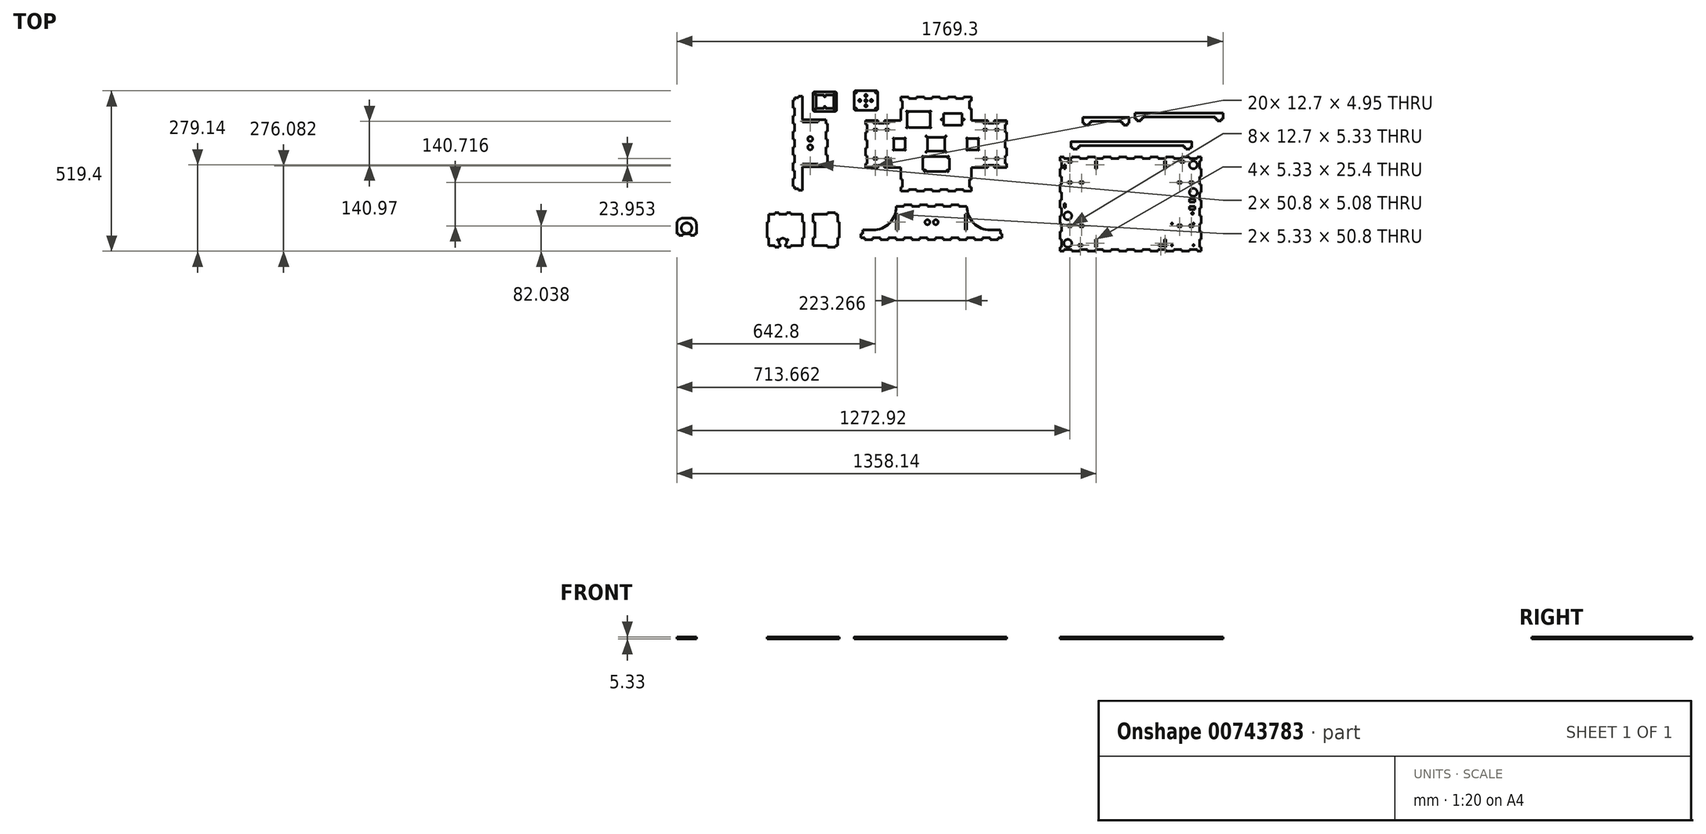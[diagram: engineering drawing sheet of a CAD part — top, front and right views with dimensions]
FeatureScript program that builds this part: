
annotation { "Feature Type Name" : "Feature", "Feature Type Description" : "" }
export const myFeature = defineFeature(function(context is Context, id is Id, definition is map)
    precondition{}
    {
        {
            assignVariable(context, id + "F0", {"name" : "T0", "anyValue" : 5.33 * mm});
        }
        {
            var Q0;
            Q0=qCreatedBy(makeId("Top.planeOp"),FACE);
            var sketch = newSketch(context, id + "F1", { "sketchPlane" : qUnion([Q0])});
            skLineSegment(sketch, "E0.bottom", {"start": v(114.3, 304.8) * mm, "end": v(139.7, 304.8) * mm});
            skLineSegment(sketch, "E0.top", {"start": v(114.3, 0) * mm, "end": v(139.7, 0) * mm});
            skLineSegment(sketch, "E0.left", {"start": v(0, 228.6) * mm, "end": v(0, 215.9) * mm});
            skLineSegment(sketch, "E0.right", {"start": v(457.2, 228.6) * mm, "end": v(457.2, 215.9) * mm});
            skLineSegment(sketch, "E1", {"start": v(0, 228.6) * mm, "end": v(40.6, 228.6) * mm});
            skLineSegment(sketch, "E2", {"start": v(114.3, 304.8) * mm, "end": v(114.3, 292.1) * mm});
            skLineSegment(sketch, "E3", {"start": v(0, 152.4) * mm, "end": v(457.2, 152.4) * mm, "construction": true});
            skLineSegment(sketch, "E4", {"start": v(228.6, 304.8) * mm, "end": v(228.6, 0) * mm, "construction": true});
            skPoint(sketch, "E5.orphan", {"position": v(0, 304.8) * mm});
            skLineSegment(sketch, "E6.MirrorCS", {"start": v(0, 76.2) * mm, "end": v(40.6, 76.2) * mm});
            skLineSegment(sketch, "E7.MirrorCS", {"start": v(114.3, 0) * mm, "end": v(114.3, 12.7) * mm});
            skLineSegment(sketch, "E8.MirrorCS", {"start": v(342.9, 304.8) * mm, "end": v(342.9, 292.1) * mm});
            skLineSegment(sketch, "E9.MirrorCS", {"start": v(457.2, 228.6) * mm, "end": v(416.6, 228.6) * mm});
            skLineSegment(sketch, "E10.MirrorCS", {"start": v(457.2, 76.2) * mm, "end": v(416.6, 76.2) * mm});
            skLineSegment(sketch, "E11.MirrorCS", {"start": v(342.9, 0) * mm, "end": v(342.9, 12.7) * mm});
            skPoint(sketch, "E12.orphan", {"position": v(0, 0) * mm});
            skPoint(sketch, "E13.orphan", {"position": v(457.2, 0) * mm});
            skPoint(sketch, "E14.orphan", {"position": v(457.2, 304.8) * mm});
            skLineSegment(sketch, "E15.bottom", {"start": v(381, 225.43) * mm, "end": v(393.7, 225.43) * mm});
            skLineSegment(sketch, "E15.top", {"start": v(381, 220.47) * mm, "end": v(393.7, 220.47) * mm});
            skLineSegment(sketch, "E15.left", {"start": v(381, 225.43) * mm, "end": v(381, 220.47) * mm});
            skLineSegment(sketch, "E15.right", {"start": v(431.8, 225.43) * mm, "end": v(431.8, 220.47) * mm});
            skLineSegment(sketch, "E16", {"start": v(393.7, 225.43) * mm, "end": v(393.7, 220.47) * mm});
            skLineSegment(sketch, "E17", {"start": v(419.1, 225.43) * mm, "end": v(419.1, 220.47) * mm});
            skLineSegment(sketch, "E18.trimOffspring", {"start": v(419.1, 225.43) * mm, "end": v(431.8, 225.43) * mm});
            skLineSegment(sketch, "E19.trimOffspring", {"start": v(419.1, 220.47) * mm, "end": v(431.8, 220.47) * mm});
            skLineSegment(sketch, "E20.0.1.0", {"start": v(381, 201.47) * mm, "end": v(393.7, 201.47) * mm});
            skLineSegment(sketch, "E20.0.1.1", {"start": v(393.7, 201.47) * mm, "end": v(393.7, 196.52) * mm});
            skLineSegment(sketch, "E20.0.1.2", {"start": v(419.1, 201.47) * mm, "end": v(419.1, 196.52) * mm});
            skLineSegment(sketch, "E20.0.1.3", {"start": v(419.1, 201.47) * mm, "end": v(431.8, 201.47) * mm});
            skLineSegment(sketch, "E20.0.1.4", {"start": v(431.8, 201.47) * mm, "end": v(431.8, 196.52) * mm});
            skLineSegment(sketch, "E20.0.1.5", {"start": v(419.1, 196.52) * mm, "end": v(431.8, 196.52) * mm});
            skLineSegment(sketch, "E20.0.1.6", {"start": v(381, 201.47) * mm, "end": v(381, 196.52) * mm});
            skLineSegment(sketch, "E20.0.1.7", {"start": v(381, 196.52) * mm, "end": v(393.7, 196.52) * mm});
            skLineSegment(sketch, "E21.MirrorCS", {"start": v(393.7, 103.33) * mm, "end": v(393.7, 108.28) * mm});
            skLineSegment(sketch, "E22.MirrorCS", {"start": v(431.8, 103.33) * mm, "end": v(431.8, 108.28) * mm});
            skLineSegment(sketch, "E23.MirrorCS", {"start": v(419.1, 79.38) * mm, "end": v(419.1, 84.33) * mm});
            skLineSegment(sketch, "E24.MirrorCS", {"start": v(381, 79.38) * mm, "end": v(381, 84.33) * mm});
            skLineSegment(sketch, "E25.MirrorCS", {"start": v(381, 103.33) * mm, "end": v(381, 108.28) * mm});
            skLineSegment(sketch, "E26.MirrorCS", {"start": v(419.1, 103.33) * mm, "end": v(419.1, 108.28) * mm});
            skLineSegment(sketch, "E27.MirrorCS", {"start": v(431.8, 79.38) * mm, "end": v(431.8, 84.33) * mm});
            skLineSegment(sketch, "E28.MirrorCS", {"start": v(393.7, 79.38) * mm, "end": v(393.7, 84.33) * mm});
            skLineSegment(sketch, "E29.MirrorCS", {"start": v(419.1, 108.28) * mm, "end": v(431.8, 108.28) * mm});
            skLineSegment(sketch, "E30.MirrorCS", {"start": v(419.1, 79.38) * mm, "end": v(431.8, 79.38) * mm});
            skLineSegment(sketch, "E31.MirrorCS", {"start": v(381, 108.28) * mm, "end": v(393.7, 108.28) * mm});
            skLineSegment(sketch, "E32.MirrorCS", {"start": v(381, 79.38) * mm, "end": v(393.7, 79.38) * mm});
            skLineSegment(sketch, "E33.MirrorCS", {"start": v(419.1, 84.33) * mm, "end": v(431.8, 84.33) * mm});
            skLineSegment(sketch, "E34.MirrorCS", {"start": v(381, 84.33) * mm, "end": v(393.7, 84.33) * mm});
            skLineSegment(sketch, "E35.MirrorCS", {"start": v(381, 103.33) * mm, "end": v(393.7, 103.33) * mm});
            skLineSegment(sketch, "E36.MirrorCS", {"start": v(419.1, 103.33) * mm, "end": v(431.8, 103.33) * mm});
            skLineSegment(sketch, "E37.MirrorCS", {"start": v(38.1, 201.47) * mm, "end": v(38.1, 196.52) * mm});
            skLineSegment(sketch, "E38.MirrorCS", {"start": v(76.2, 225.43) * mm, "end": v(76.2, 220.47) * mm});
            skLineSegment(sketch, "E39.MirrorCS", {"start": v(76.2, 201.47) * mm, "end": v(76.2, 196.52) * mm});
            skLineSegment(sketch, "E40.MirrorCS", {"start": v(38.1, 225.42) * mm, "end": v(38.1, 220.47) * mm});
            skLineSegment(sketch, "E41.MirrorCS", {"start": v(25.4, 201.47) * mm, "end": v(25.4, 196.52) * mm});
            skLineSegment(sketch, "E42.MirrorCS", {"start": v(25.4, 225.42) * mm, "end": v(25.4, 220.47) * mm});
            skLineSegment(sketch, "E43.MirrorCS", {"start": v(63.5, 201.47) * mm, "end": v(63.5, 196.52) * mm});
            skLineSegment(sketch, "E44.MirrorCS", {"start": v(76.2, 220.47) * mm, "end": v(63.5, 220.47) * mm});
            skLineSegment(sketch, "E45.MirrorCS", {"start": v(76.2, 201.47) * mm, "end": v(63.5, 201.47) * mm});
            skLineSegment(sketch, "E46.MirrorCS", {"start": v(76.2, 196.52) * mm, "end": v(63.5, 196.52) * mm});
            skLineSegment(sketch, "E47.MirrorCS", {"start": v(63.5, 225.43) * mm, "end": v(63.5, 220.47) * mm});
            skLineSegment(sketch, "E48.MirrorCS", {"start": v(76.2, 225.42) * mm, "end": v(63.5, 225.42) * mm});
            skLineSegment(sketch, "E49.MirrorCS", {"start": v(38.1, 196.52) * mm, "end": v(25.4, 196.52) * mm});
            skLineSegment(sketch, "E50.MirrorCS", {"start": v(38.1, 201.47) * mm, "end": v(25.4, 201.47) * mm});
            skLineSegment(sketch, "E51.MirrorCS", {"start": v(38.1, 220.47) * mm, "end": v(25.4, 220.47) * mm});
            skLineSegment(sketch, "E52.MirrorCS", {"start": v(38.1, 225.42) * mm, "end": v(25.4, 225.42) * mm});
            skLineSegment(sketch, "E53.MirrorCS", {"start": v(76.2, 103.33) * mm, "end": v(76.2, 108.28) * mm});
            skLineSegment(sketch, "E54.MirrorCS", {"start": v(76.2, 79.37) * mm, "end": v(76.2, 84.33) * mm});
            skLineSegment(sketch, "E55.MirrorCS", {"start": v(38.1, 79.38) * mm, "end": v(38.1, 84.33) * mm});
            skLineSegment(sketch, "E56.MirrorCS", {"start": v(25.4, 79.38) * mm, "end": v(25.4, 84.33) * mm});
            skLineSegment(sketch, "E57.MirrorCS", {"start": v(38.1, 79.38) * mm, "end": v(25.4, 79.38) * mm});
            skLineSegment(sketch, "E58.MirrorCS", {"start": v(38.1, 108.28) * mm, "end": v(25.4, 108.28) * mm});
            skLineSegment(sketch, "E59.MirrorCS", {"start": v(25.4, 103.33) * mm, "end": v(25.4, 108.28) * mm});
            skLineSegment(sketch, "E60.MirrorCS", {"start": v(38.1, 103.33) * mm, "end": v(25.4, 103.33) * mm});
            skLineSegment(sketch, "E61.MirrorCS", {"start": v(63.5, 103.33) * mm, "end": v(63.5, 108.28) * mm});
            skLineSegment(sketch, "E62.MirrorCS", {"start": v(38.1, 84.33) * mm, "end": v(25.4, 84.33) * mm});
            skLineSegment(sketch, "E63.MirrorCS", {"start": v(38.1, 103.33) * mm, "end": v(38.1, 108.28) * mm});
            skLineSegment(sketch, "E64.MirrorCS", {"start": v(63.5, 79.38) * mm, "end": v(63.5, 84.33) * mm});
            skLineSegment(sketch, "E65.MirrorCS", {"start": v(76.2, 79.38) * mm, "end": v(63.5, 79.38) * mm});
            skLineSegment(sketch, "E66.MirrorCS", {"start": v(76.2, 108.28) * mm, "end": v(63.5, 108.28) * mm});
            skLineSegment(sketch, "E67.MirrorCS", {"start": v(76.2, 84.33) * mm, "end": v(63.5, 84.33) * mm});
            skLineSegment(sketch, "E68.MirrorCS", {"start": v(76.2, 103.33) * mm, "end": v(63.5, 103.33) * mm});
            skCircle(sketch, "E69.1.0", {"center": v(91.2, 133.9) * mm, "radius": 1.46 * mm});
            skCircle(sketch, "E69.1.1", {"center": v(128.2, 133.9) * mm, "radius": 1.46 * mm});
            skCircle(sketch, "E69.1.2", {"center": v(128.2, 170.9) * mm, "radius": 1.56 * mm});
            skCircle(sketch, "E69.1.3", {"center": v(91.2, 170.9) * mm, "radius": 1.46 * mm});
            skLineSegment(sketch, "E70.left", {"start": v(91.2, 166.94) * mm, "end": v(91.2, 137.86) * mm});
            skLineSegment(sketch, "E70.right", {"start": v(128.2, 166.84) * mm, "end": v(128.2, 137.86) * mm});
            skArc(sketch, "E71.0", {"start": v(91.2, 166.94) * mm, "mid": v(94, 168.1) * mm, "end": v(95.16, 170.9) * mm});
            skArc(sketch, "E72.0", {"start": v(124.14, 170.9) * mm, "mid": v(125.33, 168.03) * mm, "end": v(128.2, 166.84) * mm});
            skArc(sketch, "E73.0", {"start": v(95.16, 133.9) * mm, "mid": v(94, 136.7) * mm, "end": v(91.2, 137.86) * mm});
            skArc(sketch, "E74.0", {"start": v(128.2, 137.86) * mm, "mid": v(125.4, 136.7) * mm, "end": v(124.24, 133.9) * mm});
            skLineSegment(sketch, "E75.trimOffspring", {"start": v(95.16, 170.9) * mm, "end": v(124.14, 170.9) * mm});
            skLineSegment(sketch, "E76.trimOffspring", {"start": v(95.16, 133.9) * mm, "end": v(124.24, 133.9) * mm});
            skCircle(sketch, "E77.MirrorC", {"center": v(329, 133.9) * mm, "radius": 1.46 * mm});
            skArc(sketch, "E78.MirrorCS", {"start": v(329, 137.86) * mm, "mid": v(331.8, 136.7) * mm, "end": v(332.96, 133.9) * mm});
            skArc(sketch, "E79.MirrorCS", {"start": v(362.04, 133.9) * mm, "mid": v(363.2, 136.7) * mm, "end": v(366, 137.86) * mm});
            skArc(sketch, "E80.MirrorCS", {"start": v(366, 166.94) * mm, "mid": v(363.2, 168.1) * mm, "end": v(362.04, 170.9) * mm});
            skArc(sketch, "E81.MirrorCS", {"start": v(333.06, 170.9) * mm, "mid": v(331.87, 168.03) * mm, "end": v(329, 166.84) * mm});
            skCircle(sketch, "E82.MirrorC", {"center": v(366, 133.9) * mm, "radius": 1.46 * mm});
            skCircle(sketch, "E83.MirrorC", {"center": v(329, 170.9) * mm, "radius": 1.56 * mm});
            skCircle(sketch, "E84.MirrorC", {"center": v(366, 170.9) * mm, "radius": 1.46 * mm});
            skLineSegment(sketch, "E85.MirrorCS", {"start": v(329, 166.84) * mm, "end": v(329, 137.86) * mm});
            skLineSegment(sketch, "E86.MirrorCS", {"start": v(366, 166.94) * mm, "end": v(366, 137.86) * mm});
            skLineSegment(sketch, "E87.MirrorCS", {"start": v(362.04, 133.9) * mm, "end": v(332.96, 133.9) * mm});
            skLineSegment(sketch, "E88.MirrorCS", {"start": v(362.04, 170.9) * mm, "end": v(333.06, 170.9) * mm});
            skCircle(sketch, "E89", {"center": v(268.36, 112.4) * mm, "radius": 1.59 * mm});
            skCircle(sketch, "E90", {"center": v(185.8, 112.4) * mm, "radius": 1.59 * mm});
            skCircle(sketch, "E91", {"center": v(192.16, 64.14) * mm, "radius": 1.59 * mm});
            skCircle(sketch, "E92", {"center": v(267.09, 64.14) * mm, "radius": 1.59 * mm});
            skLineSegment(sketch, "E93.top", {"start": v(139.7, 299.47) * mm, "end": v(165.1, 299.47) * mm});
            skLineSegment(sketch, "E93.left", {"start": v(139.7, 304.8) * mm, "end": v(139.7, 299.47) * mm});
            skLineSegment(sketch, "E93.right", {"start": v(165.1, 304.8) * mm, "end": v(165.1, 299.47) * mm});
            skLineSegment(sketch, "E94.1.0.0", {"start": v(215.9, 304.8) * mm, "end": v(215.9, 299.47) * mm});
            skLineSegment(sketch, "E94.1.0.1", {"start": v(190.5, 299.47) * mm, "end": v(215.9, 299.47) * mm});
            skLineSegment(sketch, "E94.1.0.2", {"start": v(190.5, 304.8) * mm, "end": v(190.5, 299.47) * mm});
            skLineSegment(sketch, "E94.2.0.0", {"start": v(266.7, 304.8) * mm, "end": v(266.7, 299.47) * mm});
            skLineSegment(sketch, "E94.2.0.1", {"start": v(241.3, 299.47) * mm, "end": v(266.7, 299.47) * mm});
            skLineSegment(sketch, "E94.2.0.2", {"start": v(241.3, 304.8) * mm, "end": v(241.3, 299.47) * mm});
            skLineSegment(sketch, "E94.3.0.0", {"start": v(317.5, 304.8) * mm, "end": v(317.5, 299.47) * mm});
            skLineSegment(sketch, "E94.3.0.1", {"start": v(292.1, 299.47) * mm, "end": v(317.5, 299.47) * mm});
            skLineSegment(sketch, "E94.3.0.2", {"start": v(292.1, 304.8) * mm, "end": v(292.1, 299.47) * mm});
            skLineSegment(sketch, "E94.direction1", {"start": v(165.1, 299.47) * mm, "end": v(215.9, 299.47) * mm, "construction": true});
            skLineSegment(sketch, "E95.trimOffspring", {"start": v(215.9, 304.8) * mm, "end": v(241.3, 304.8) * mm});
            skLineSegment(sketch, "E96.trimOffspring", {"start": v(165.1, 304.8) * mm, "end": v(190.5, 304.8) * mm});
            skLineSegment(sketch, "E97.trimOffspring", {"start": v(266.7, 304.8) * mm, "end": v(292.1, 304.8) * mm});
            skLineSegment(sketch, "E98.trimOffspring", {"start": v(317.5, 304.8) * mm, "end": v(342.9, 304.8) * mm});
            skLineSegment(sketch, "E99.MirrorCS", {"start": v(215.9, 0) * mm, "end": v(215.9, 5.33) * mm});
            skLineSegment(sketch, "E100.MirrorCS", {"start": v(165.1, 0) * mm, "end": v(165.1, 5.33) * mm});
            skLineSegment(sketch, "E101.MirrorCS", {"start": v(317.5, 0) * mm, "end": v(317.5, 5.33) * mm});
            skLineSegment(sketch, "E102.MirrorCS", {"start": v(241.3, 0) * mm, "end": v(241.3, 5.33) * mm});
            skLineSegment(sketch, "E103.MirrorCS", {"start": v(139.7, 0) * mm, "end": v(139.7, 5.33) * mm});
            skLineSegment(sketch, "E104.MirrorCS", {"start": v(292.1, 0) * mm, "end": v(292.1, 5.33) * mm});
            skLineSegment(sketch, "E105.MirrorCS", {"start": v(342.9, 0) * mm, "end": v(342.9, 5.33) * mm});
            skLineSegment(sketch, "E106.MirrorCS", {"start": v(190.5, 0) * mm, "end": v(190.5, 5.33) * mm});
            skLineSegment(sketch, "E107.MirrorCS", {"start": v(266.7, 0) * mm, "end": v(266.7, 5.33) * mm});
            skLineSegment(sketch, "E108.MirrorCS", {"start": v(190.5, 5.33) * mm, "end": v(215.9, 5.33) * mm});
            skLineSegment(sketch, "E109.MirrorCS", {"start": v(139.7, 5.33) * mm, "end": v(165.1, 5.33) * mm});
            skLineSegment(sketch, "E110.MirrorCS", {"start": v(292.1, 5.33) * mm, "end": v(317.5, 5.33) * mm});
            skLineSegment(sketch, "E111.MirrorCS", {"start": v(215.9, 0) * mm, "end": v(241.3, 0) * mm});
            skLineSegment(sketch, "E112.MirrorCS", {"start": v(241.3, 5.33) * mm, "end": v(266.7, 5.33) * mm});
            skLineSegment(sketch, "E113.MirrorCS", {"start": v(165.1, 0) * mm, "end": v(190.5, 0) * mm});
            skLineSegment(sketch, "E114.MirrorCS", {"start": v(165.1, 5.33) * mm, "end": v(215.9, 5.33) * mm, "construction": true});
            skLineSegment(sketch, "E115.MirrorCS", {"start": v(266.7, 0) * mm, "end": v(292.1, 0) * mm});
            skLineSegment(sketch, "E116.MirrorCS", {"start": v(317.5, 0) * mm, "end": v(342.9, 0) * mm});
            skLineSegment(sketch, "E117.bottom", {"start": v(0, 215.9) * mm, "end": v(5.33, 215.9) * mm});
            skLineSegment(sketch, "E117.top", {"start": v(0, 190.5) * mm, "end": v(5.33, 190.5) * mm});
            skLineSegment(sketch, "E117.right", {"start": v(5.33, 215.9) * mm, "end": v(5.33, 190.5) * mm});
            skLineSegment(sketch, "E118.0.1.0", {"start": v(0, 165.1) * mm, "end": v(5.33, 165.1) * mm});
            skLineSegment(sketch, "E118.0.1.1", {"start": v(5.33, 165.1) * mm, "end": v(5.33, 139.7) * mm});
            skLineSegment(sketch, "E118.0.1.2", {"start": v(0, 139.7) * mm, "end": v(5.33, 139.7) * mm});
            skLineSegment(sketch, "E118.0.2.0", {"start": v(0, 114.3) * mm, "end": v(5.33, 114.3) * mm});
            skLineSegment(sketch, "E118.0.2.1", {"start": v(5.33, 114.3) * mm, "end": v(5.33, 88.9) * mm});
            skLineSegment(sketch, "E118.0.2.2", {"start": v(0, 88.9) * mm, "end": v(5.33, 88.9) * mm});
            skLineSegment(sketch, "E118.direction2", {"start": v(0, 190.5) * mm, "end": v(0, 165.1) * mm, "construction": true});
            skLineSegment(sketch, "E119.trimOffspring", {"start": v(0, 139.7) * mm, "end": v(0, 114.3) * mm});
            skLineSegment(sketch, "E120.trimOffspring", {"start": v(0, 190.5) * mm, "end": v(0, 165.1) * mm});
            skLineSegment(sketch, "E121.trimOffspring", {"start": v(0, 88.9) * mm, "end": v(0, 76.2) * mm});
            skLineSegment(sketch, "E122.MirrorCS", {"start": v(457.2, 215.9) * mm, "end": v(432.2, 215.9) * mm, "construction": true});
            skLineSegment(sketch, "E123.MirrorCS", {"start": v(451.87, 215.9) * mm, "end": v(451.87, 190.5) * mm});
            skPoint(sketch, "E124.orphan", {"position": v(25, 215.9) * mm});
            skLineSegment(sketch, "E125.MirrorCS", {"start": v(457.2, 215.9) * mm, "end": v(451.87, 215.9) * mm});
            skLineSegment(sketch, "E126.MirrorCS", {"start": v(457.2, 190.5) * mm, "end": v(451.87, 190.5) * mm});
            skLineSegment(sketch, "E127.MirrorCS", {"start": v(457.2, 165.1) * mm, "end": v(451.87, 165.1) * mm});
            skLineSegment(sketch, "E128.MirrorCS", {"start": v(451.87, 165.1) * mm, "end": v(451.87, 139.7) * mm});
            skLineSegment(sketch, "E129.MirrorCS", {"start": v(457.2, 139.7) * mm, "end": v(451.87, 139.7) * mm});
            skLineSegment(sketch, "E130.MirrorCS", {"start": v(457.2, 114.3) * mm, "end": v(451.87, 114.3) * mm});
            skLineSegment(sketch, "E131.MirrorCS", {"start": v(451.87, 114.3) * mm, "end": v(451.87, 88.9) * mm});
            skLineSegment(sketch, "E132.MirrorCS", {"start": v(457.2, 88.9) * mm, "end": v(451.87, 88.9) * mm});
            skLineSegment(sketch, "E133.trimOffspring", {"start": v(457.2, 139.7) * mm, "end": v(457.2, 114.3) * mm});
            skLineSegment(sketch, "E134.trimOffspring", {"start": v(457.2, 88.9) * mm, "end": v(457.2, 76.2) * mm});
            skLineSegment(sketch, "E135.trimOffspring", {"start": v(457.2, 190.5) * mm, "end": v(457.2, 165.1) * mm});
            skPoint(sketch, "E136.trimOffspring.start.orphan", {"position": v(368.3, 304.8) * mm});
            skLineSegment(sketch, "E137.bottom", {"start": v(114.3, 38.1) * mm, "end": v(119.63, 38.1) * mm});
            skLineSegment(sketch, "E137.top", {"start": v(114.3, 12.7) * mm, "end": v(119.63, 12.7) * mm});
            skLineSegment(sketch, "E137.right", {"start": v(119.63, 38.1) * mm, "end": v(119.63, 12.7) * mm});
            skLineSegment(sketch, "E138.trimOffspring", {"start": v(114.3, 38.1) * mm, "end": v(114.3, 76.2) * mm});
            skLineSegment(sketch, "E139.MirrorCS", {"start": v(114.3, 292.1) * mm, "end": v(119.63, 292.1) * mm});
            skLineSegment(sketch, "E140.MirrorCS", {"start": v(114.3, 266.7) * mm, "end": v(119.63, 266.7) * mm});
            skLineSegment(sketch, "E141.MirrorCS", {"start": v(119.63, 266.7) * mm, "end": v(119.63, 292.1) * mm});
            skLineSegment(sketch, "E142.MirrorCS", {"start": v(342.9, 292.1) * mm, "end": v(337.57, 292.1) * mm});
            skLineSegment(sketch, "E143.MirrorCS", {"start": v(337.57, 266.7) * mm, "end": v(337.57, 292.1) * mm});
            skLineSegment(sketch, "E144.MirrorCS", {"start": v(342.9, 266.7) * mm, "end": v(337.57, 266.7) * mm});
            skLineSegment(sketch, "E145.MirrorCS", {"start": v(342.9, 38.1) * mm, "end": v(337.57, 38.1) * mm});
            skLineSegment(sketch, "E146.MirrorCS", {"start": v(337.57, 38.1) * mm, "end": v(337.57, 12.7) * mm});
            skLineSegment(sketch, "E147.MirrorCS", {"start": v(342.9, 12.7) * mm, "end": v(337.57, 12.7) * mm});
            skLineSegment(sketch, "E148.trimOffspring", {"start": v(342.9, 38.1) * mm, "end": v(342.9, 76.2) * mm});
            skPoint(sketch, "E149.MirrorCS.start.orphan", {"position": v(368.3, 0) * mm});
            skLineSegment(sketch, "E150.trimOffspring", {"start": v(342.9, 266.7) * mm, "end": v(342.9, 228.6) * mm});
            skLineSegment(sketch, "E151.trimOffspring", {"start": v(114.3, 266.7) * mm, "end": v(114.3, 228.6) * mm});
            skCircle(sketch, "E152", {"center": v(246.46, 232.2) * mm, "radius": 1.6 * mm});
            skCircle(sketch, "E153", {"center": v(318.85, 232.2) * mm, "radius": 1.59 * mm});
            skLineSegment(sketch, "E154.top", {"start": v(40.6, 220.32) * mm, "end": v(61, 220.32) * mm});
            skLineSegment(sketch, "E154.left", {"start": v(40.6, 228.6) * mm, "end": v(40.6, 220.32) * mm});
            skLineSegment(sketch, "E154.right", {"start": v(61, 228.6) * mm, "end": v(61, 220.32) * mm});
            skLineSegment(sketch, "E155.trimOffspring", {"start": v(61, 228.6) * mm, "end": v(114.3, 228.6) * mm});
            skLineSegment(sketch, "E156.MirrorCS", {"start": v(416.6, 228.6) * mm, "end": v(416.6, 220.32) * mm});
            skLineSegment(sketch, "E157.MirrorCS", {"start": v(416.6, 220.32) * mm, "end": v(396.2, 220.32) * mm});
            skLineSegment(sketch, "E158.MirrorCS", {"start": v(396.2, 228.6) * mm, "end": v(396.2, 220.32) * mm});
            skLineSegment(sketch, "E159.trimOffspring", {"start": v(396.2, 228.6) * mm, "end": v(342.9, 228.6) * mm});
            skLineSegment(sketch, "E160.MirrorCS", {"start": v(396.2, 76.2) * mm, "end": v(396.2, 84.48) * mm});
            skLineSegment(sketch, "E161.MirrorCS", {"start": v(416.6, 84.48) * mm, "end": v(396.2, 84.48) * mm});
            skLineSegment(sketch, "E162.MirrorCS", {"start": v(416.6, 76.2) * mm, "end": v(416.6, 84.48) * mm});
            skLineSegment(sketch, "E163.MirrorCS", {"start": v(61, 76.2) * mm, "end": v(61, 84.48) * mm});
            skLineSegment(sketch, "E164.MirrorCS", {"start": v(40.6, 84.48) * mm, "end": v(61, 84.48) * mm});
            skLineSegment(sketch, "E165.MirrorCS", {"start": v(40.6, 76.2) * mm, "end": v(40.6, 84.48) * mm});
            skLineSegment(sketch, "E166.trimOffspring", {"start": v(61, 76.2) * mm, "end": v(114.3, 76.2) * mm});
            skLineSegment(sketch, "E167.trimOffspring", {"start": v(396.2, 76.2) * mm, "end": v(342.9, 76.2) * mm});
            skCircle(sketch, "E168", {"center": v(134.46, 258.2) * mm, "radius": 1.59 * mm});
            skLineSegment(sketch, "E169.left", {"start": v(134.46, 253.2) * mm, "end": v(134.46, 211.2) * mm});
            skCircle(sketch, "E170", {"center": v(210.46, 258.2) * mm, "radius": 1.59 * mm});
            skCircle(sketch, "E171", {"center": v(210.46, 206.2) * mm, "radius": 1.6 * mm});
            skCircle(sketch, "E172", {"center": v(134.46, 206.2) * mm, "radius": 1.6 * mm});
            skArc(sketch, "E173", {"start": v(134.46, 253.2) * mm, "mid": v(138, 254.67) * mm, "end": v(139.46, 258.2) * mm});
            skArc(sketch, "E174", {"start": v(139.46, 206.2) * mm, "mid": v(138, 209.74) * mm, "end": v(134.46, 211.2) * mm});
            skArc(sketch, "E175", {"start": v(205.46, 206.2) * mm, "mid": v(206.93, 209.74) * mm, "end": v(210.46, 211.2) * mm});
            skArc(sketch, "E176", {"start": v(210.46, 253.2) * mm, "mid": v(206.93, 254.67) * mm, "end": v(205.46, 258.2) * mm});
            skLineSegment(sketch, "E177.trimOffspring", {"start": v(210.46, 253.2) * mm, "end": v(210.46, 211.2) * mm});
            skLineSegment(sketch, "E178.trimOffspring", {"start": v(139.46, 206.2) * mm, "end": v(205.46, 206.2) * mm});
            skLineSegment(sketch, "E179", {"start": v(139.46, 258.2) * mm, "end": v(205.46, 258.2) * mm});
            skLineSegment(sketch, "E180", {"start": v(134.46, 232.2) * mm, "end": v(210.46, 232.2) * mm, "construction": true});
            skLineSegment(sketch, "E181.bottom", {"start": v(252.81, 251.25) * mm, "end": v(312.5, 251.25) * mm});
            skLineSegment(sketch, "E181.top", {"start": v(252.81, 213.15) * mm, "end": v(312.5, 213.15) * mm});
            skLineSegment(sketch, "E181.left", {"start": v(252.81, 251.25) * mm, "end": v(252.81, 213.15) * mm});
            skLineSegment(sketch, "E181.right", {"start": v(312.5, 251.25) * mm, "end": v(312.5, 213.15) * mm});
            skLineSegment(sketch, "E182.bottom", {"start": v(190.8, 112.4) * mm, "end": v(263.36, 112.4) * mm});
            skLineSegment(sketch, "E182.left", {"start": v(185.8, 107.4) * mm, "end": v(185.8, 69.14) * mm});
            skLineSegment(sketch, "E182.right", {"start": v(272.2, 107.4) * mm, "end": v(272.2, 69.14) * mm});
            skArc(sketch, "E183", {"start": v(190.8, 112.4) * mm, "mid": v(189.34, 108.86) * mm, "end": v(185.8, 107.4) * mm});
            skArc(sketch, "E184", {"start": v(197.16, 64.14) * mm, "mid": v(195.7, 67.68) * mm, "end": v(192.16, 69.14) * mm});
            skArc(sketch, "E185", {"start": v(262.09, 64.14) * mm, "mid": v(263.55, 67.68) * mm, "end": v(267.09, 69.14) * mm});
            skArc(sketch, "E186", {"start": v(263.36, 112.4) * mm, "mid": v(264.82, 108.86) * mm, "end": v(268.36, 107.4) * mm});
            skLineSegment(sketch, "E187", {"start": v(192.16, 69.14) * mm, "end": v(185.8, 69.14) * mm});
            skLineSegment(sketch, "E188", {"start": v(267.09, 69.14) * mm, "end": v(272.2, 69.14) * mm});
            skLineSegment(sketch, "E189", {"start": v(268.36, 107.4) * mm, "end": v(272.2, 107.4) * mm});
            skLineSegment(sketch, "E190.trimOffspring", {"start": v(197.16, 64.14) * mm, "end": v(262.09, 64.14) * mm});
            skPoint(sketch, "E191.orphan", {"position": v(272.2, 64.14) * mm});
            skLineSegment(sketch, "E192.bottom", {"start": v(258.76, 177.8) * mm, "end": v(198.44, 177.8) * mm, "construction": true});
            skLineSegment(sketch, "E192.top", {"start": v(258.76, 127) * mm, "end": v(198.44, 127) * mm, "construction": true});
            skLineSegment(sketch, "E192.left", {"start": v(260.35, 176.21) * mm, "end": v(260.35, 128.6) * mm, "construction": true});
            skLineSegment(sketch, "E192.right", {"start": v(196.85, 176.21) * mm, "end": v(196.85, 128.6) * mm, "construction": true});
            skPoint(sketch, "E192.middle", {"position": v(228.6, 152.4) * mm});
            skCircle(sketch, "E193", {"center": v(196.85, 127) * mm, "radius": 1.6 * mm});
            skCircle(sketch, "E194", {"center": v(260.35, 127) * mm, "radius": 1.59 * mm});
            skCircle(sketch, "E195", {"center": v(260.35, 177.8) * mm, "radius": 1.6 * mm});
            skCircle(sketch, "E196", {"center": v(196.85, 177.8) * mm, "radius": 1.59 * mm});
            skLineSegment(sketch, "E197.bottom", {"start": v(200.73, 174.73) * mm, "end": v(256.47, 174.73) * mm});
            skLineSegment(sketch, "E197.top", {"start": v(200.73, 130.07) * mm, "end": v(256.47, 130.07) * mm});
            skLineSegment(sketch, "E197.left", {"start": v(200.73, 174.73) * mm, "end": v(200.73, 130.07) * mm});
            skLineSegment(sketch, "E197.right", {"start": v(256.47, 174.73) * mm, "end": v(256.47, 130.07) * mm});
            skSolve(sketch);
        }
        {
            var Q0;
            Q0=makeQuery(id+"F1.imprint","IMPRINT",FACE,{"disambiguationData":[TD([[makeQuery(id+"F1.imprint","IMPRINT",EDGE,{"derivedFrom":sQuery(id+"F1.wireOp",EDGE,"E0.bottom")}),-1.0]])]});
            extrude(context, id + "F2", {"entities" : qUnion([Q0]), "depth" : getVariable(context, 'T0'), "offsetDistance" : 25 * mm});
        }
        {
            var Q0;
            Q0=qCreatedBy(makeId("Top.planeOp"),FACE);
            var sketch = newSketch(context, id + "F3", { "sketchPlane" : qUnion([Q0])});
            skLineSegment(sketch, "E198.bottom", {"start": v(442.84, -151.33) * mm, "end": v(430.14, -151.33) * mm});
            skLineSegment(sketch, "E198.left", {"start": v(442.84, -151.33) * mm, "end": v(442.84, -138.63) * mm});
            skLineSegment(sketch, "E198.right", {"start": v(-14.36, -151.33) * mm, "end": v(-14.36, -138.63) * mm});
            skLineSegment(sketch, "E199", {"start": v(-14.36, -100.53) * mm, "end": v(442.84, -100.53) * mm, "construction": true});
            skLineSegment(sketch, "E200", {"start": v(214.24, -49.73) * mm, "end": v(214.24, -151.33) * mm, "construction": true});
            skLineSegment(sketch, "E201.top", {"start": v(125.34, -44.4) * mm, "end": v(150.74, -44.4) * mm});
            skLineSegment(sketch, "E201.left", {"start": v(125.34, -49.73) * mm, "end": v(125.34, -44.4) * mm});
            skLineSegment(sketch, "E201.right", {"start": v(150.74, -49.73) * mm, "end": v(150.74, -44.4) * mm});
            skLineSegment(sketch, "E202.1.0.0", {"start": v(176.14, -44.4) * mm, "end": v(201.54, -44.4) * mm});
            skLineSegment(sketch, "E202.1.0.1", {"start": v(176.14, -49.73) * mm, "end": v(176.14, -44.4) * mm});
            skLineSegment(sketch, "E202.1.0.2", {"start": v(201.54, -49.73) * mm, "end": v(201.54, -44.4) * mm});
            skLineSegment(sketch, "E202.2.0.0", {"start": v(226.94, -44.4) * mm, "end": v(252.34, -44.4) * mm});
            skLineSegment(sketch, "E202.2.0.1", {"start": v(226.94, -49.73) * mm, "end": v(226.94, -44.4) * mm});
            skLineSegment(sketch, "E202.2.0.2", {"start": v(252.34, -49.73) * mm, "end": v(252.34, -44.4) * mm});
            skLineSegment(sketch, "E202.3.0.0", {"start": v(277.74, -44.4) * mm, "end": v(303.14, -44.4) * mm});
            skLineSegment(sketch, "E202.3.0.1", {"start": v(277.74, -49.73) * mm, "end": v(277.74, -44.4) * mm});
            skLineSegment(sketch, "E202.3.0.2", {"start": v(303.14, -49.73) * mm, "end": v(303.14, -44.4) * mm});
            skLineSegment(sketch, "E202.direction1", {"start": v(150.74, -44.4) * mm, "end": v(201.54, -44.4) * mm, "construction": true});
            skArc(sketch, "E203", {"start": v(99.94, -49.73) * mm, "mid": v(77.63, -103.61) * mm, "end": v(23.74, -125.93) * mm});
            skLineSegment(sketch, "E204", {"start": v(23.74, -125.93) * mm, "end": v(-9.02, -125.93) * mm});
            skPoint(sketch, "E205.orphan", {"position": v(-14.36, -49.73) * mm});
            skLineSegment(sketch, "E206.trimOffspring", {"start": v(176.14, -49.73) * mm, "end": v(150.74, -49.73) * mm});
            skLineSegment(sketch, "E207.trimOffspring", {"start": v(125.34, -49.73) * mm, "end": v(99.94, -49.73) * mm});
            skLineSegment(sketch, "E208.trimOffspring", {"start": v(226.94, -49.73) * mm, "end": v(201.54, -49.73) * mm});
            skLineSegment(sketch, "E209.trimOffspring", {"start": v(277.74, -49.73) * mm, "end": v(252.34, -49.73) * mm});
            skLineSegment(sketch, "E210.trimOffspring", {"start": v(328.54, -49.73) * mm, "end": v(303.14, -49.73) * mm});
            skArc(sketch, "E211.MirrorCS", {"start": v(328.54, -49.73) * mm, "mid": v(350.86, -103.61) * mm, "end": v(404.74, -125.93) * mm});
            skLineSegment(sketch, "E212.MirrorCS", {"start": v(404.74, -125.93) * mm, "end": v(437.51, -125.93) * mm});
            skPoint(sketch, "E213.orphan", {"position": v(442.84, -49.73) * mm});
            skLineSegment(sketch, "E214.top", {"start": v(437.51, -138.63) * mm, "end": v(442.84, -138.63) * mm});
            skLineSegment(sketch, "E214.left", {"start": v(437.51, -125.93) * mm, "end": v(437.51, -138.63) * mm});
            skPoint(sketch, "E215.orphan", {"position": v(442.84, -125.93) * mm});
            skLineSegment(sketch, "E216.MirrorCS", {"start": v(-9.02, -125.93) * mm, "end": v(-9.02, -138.63) * mm});
            skLineSegment(sketch, "E217.MirrorCS", {"start": v(-9.02, -138.63) * mm, "end": v(-14.36, -138.63) * mm});
            skPoint(sketch, "E218.orphan", {"position": v(-14.36, -125.93) * mm});
            skLineSegment(sketch, "E219.top", {"start": v(-1.66, -156.67) * mm, "end": v(23.74, -156.67) * mm});
            skLineSegment(sketch, "E219.left", {"start": v(-1.66, -151.33) * mm, "end": v(-1.66, -156.67) * mm});
            skLineSegment(sketch, "E219.right", {"start": v(23.74, -151.33) * mm, "end": v(23.74, -156.67) * mm});
            skLineSegment(sketch, "E220.trimOffspring", {"start": v(-1.66, -151.33) * mm, "end": v(-14.36, -151.33) * mm});
            skLineSegment(sketch, "E221.1.0.0", {"start": v(74.54, -151.33) * mm, "end": v(74.54, -156.67) * mm});
            skLineSegment(sketch, "E221.1.0.1", {"start": v(49.14, -151.33) * mm, "end": v(49.14, -156.67) * mm});
            skLineSegment(sketch, "E221.1.0.2", {"start": v(49.14, -156.67) * mm, "end": v(74.54, -156.67) * mm});
            skLineSegment(sketch, "E221.2.0.0", {"start": v(125.34, -151.33) * mm, "end": v(125.34, -156.67) * mm});
            skLineSegment(sketch, "E221.2.0.1", {"start": v(99.94, -151.33) * mm, "end": v(99.94, -156.67) * mm});
            skLineSegment(sketch, "E221.2.0.2", {"start": v(99.94, -156.67) * mm, "end": v(125.34, -156.67) * mm});
            skLineSegment(sketch, "E221.3.0.0", {"start": v(176.14, -151.33) * mm, "end": v(176.14, -156.67) * mm});
            skLineSegment(sketch, "E221.3.0.1", {"start": v(150.74, -151.33) * mm, "end": v(150.74, -156.67) * mm});
            skLineSegment(sketch, "E221.3.0.2", {"start": v(150.74, -156.67) * mm, "end": v(176.14, -156.67) * mm});
            skLineSegment(sketch, "E221.4.0.0", {"start": v(226.94, -151.33) * mm, "end": v(226.94, -156.67) * mm});
            skLineSegment(sketch, "E221.4.0.1", {"start": v(201.54, -151.33) * mm, "end": v(201.54, -156.67) * mm});
            skLineSegment(sketch, "E221.4.0.2", {"start": v(201.54, -156.67) * mm, "end": v(226.94, -156.67) * mm});
            skLineSegment(sketch, "E221.5.0.0", {"start": v(277.74, -151.33) * mm, "end": v(277.74, -156.67) * mm});
            skLineSegment(sketch, "E221.5.0.1", {"start": v(252.34, -151.33) * mm, "end": v(252.34, -156.67) * mm});
            skLineSegment(sketch, "E221.5.0.2", {"start": v(252.34, -156.67) * mm, "end": v(277.74, -156.67) * mm});
            skLineSegment(sketch, "E221.6.0.0", {"start": v(328.54, -151.33) * mm, "end": v(328.54, -156.67) * mm});
            skLineSegment(sketch, "E221.6.0.1", {"start": v(303.14, -151.33) * mm, "end": v(303.14, -156.67) * mm});
            skLineSegment(sketch, "E221.6.0.2", {"start": v(303.14, -156.67) * mm, "end": v(328.54, -156.67) * mm});
            skLineSegment(sketch, "E221.7.0.0", {"start": v(379.34, -151.33) * mm, "end": v(379.34, -156.67) * mm});
            skLineSegment(sketch, "E221.7.0.1", {"start": v(353.94, -151.33) * mm, "end": v(353.94, -156.67) * mm});
            skLineSegment(sketch, "E221.7.0.2", {"start": v(353.94, -156.67) * mm, "end": v(379.34, -156.67) * mm});
            skLineSegment(sketch, "E221.8.0.0", {"start": v(430.14, -151.33) * mm, "end": v(430.14, -156.67) * mm});
            skLineSegment(sketch, "E221.8.0.1", {"start": v(404.74, -151.33) * mm, "end": v(404.74, -156.67) * mm});
            skLineSegment(sketch, "E221.8.0.2", {"start": v(404.74, -156.67) * mm, "end": v(430.14, -156.67) * mm});
            skLineSegment(sketch, "E221.direction1", {"start": v(23.74, -156.67) * mm, "end": v(74.54, -156.67) * mm, "construction": true});
            skLineSegment(sketch, "E222.trimOffspring", {"start": v(49.14, -151.33) * mm, "end": v(23.74, -151.33) * mm});
            skLineSegment(sketch, "E223.trimOffspring", {"start": v(99.94, -151.33) * mm, "end": v(74.54, -151.33) * mm});
            skLineSegment(sketch, "E224.trimOffspring", {"start": v(150.74, -151.33) * mm, "end": v(125.34, -151.33) * mm});
            skLineSegment(sketch, "E225.trimOffspring", {"start": v(201.54, -151.33) * mm, "end": v(176.14, -151.33) * mm});
            skLineSegment(sketch, "E226.trimOffspring", {"start": v(252.34, -151.33) * mm, "end": v(226.94, -151.33) * mm});
            skLineSegment(sketch, "E227.trimOffspring", {"start": v(303.14, -151.33) * mm, "end": v(277.74, -151.33) * mm});
            skLineSegment(sketch, "E228.trimOffspring", {"start": v(353.94, -151.33) * mm, "end": v(328.54, -151.33) * mm});
            skLineSegment(sketch, "E229.trimOffspring", {"start": v(404.74, -151.33) * mm, "end": v(379.34, -151.33) * mm});
            skLineSegment(sketch, "E230.bottom", {"start": v(99.94, -75.13) * mm, "end": v(105.28, -75.13) * mm});
            skLineSegment(sketch, "E230.top", {"start": v(99.94, -125.93) * mm, "end": v(105.28, -125.93) * mm});
            skLineSegment(sketch, "E230.left", {"start": v(99.94, -75.13) * mm, "end": v(99.94, -125.93) * mm});
            skLineSegment(sketch, "E230.right", {"start": v(105.28, -75.13) * mm, "end": v(105.28, -125.93) * mm});
            skLineSegment(sketch, "E231.MirrorCS", {"start": v(328.54, -75.13) * mm, "end": v(328.54, -125.93) * mm});
            skLineSegment(sketch, "E232.MirrorCS", {"start": v(323.21, -75.13) * mm, "end": v(323.21, -125.93) * mm});
            skLineSegment(sketch, "E233.MirrorCS", {"start": v(328.54, -75.13) * mm, "end": v(323.21, -75.13) * mm});
            skLineSegment(sketch, "E234.MirrorCS", {"start": v(328.54, -125.93) * mm, "end": v(323.21, -125.93) * mm});
            skCircle(sketch, "E235", {"center": v(200.74, -100.53) * mm, "radius": 8 * mm});
            skCircle(sketch, "E236.MirrorC", {"center": v(227.74, -100.53) * mm, "radius": 8 * mm});
            skSolve(sketch);
        }
        {
            var Q0;
            Q0 = qSketchRegion(id + "F3", true);
            extrude(context, id + "F4", {"entities" : qUnion([Q0]), "depth" : getVariable(context, 'T0'), "offsetDistance" : 25 * mm});
        }
        {
            var Q0;
            Q0=qCreatedBy(makeId("Top.planeOp"),FACE);
            var sketch = newSketch(context, id + "F5", { "sketchPlane" : qUnion([Q0])});
            skLineSegment(sketch, "E237.bottom", {"start": v(-217.07, 307.8) * mm, "end": v(-204.37, 307.8) * mm});
            skLineSegment(sketch, "E237.top", {"start": v(-217.07, 3) * mm, "end": v(-204.37, 3) * mm});
            skLineSegment(sketch, "E237.left", {"start": v(-229.77, 302.46) * mm, "end": v(-229.77, 295.1) * mm});
            skLineSegment(sketch, "E237.right", {"start": v(-128.17, 231.6) * mm, "end": v(-128.17, 218.9) * mm});
            skLineSegment(sketch, "E238.top", {"start": v(-204.37, 79.2) * mm, "end": v(-128.17, 79.2) * mm});
            skLineSegment(sketch, "E238.left", {"start": v(-204.37, 3) * mm, "end": v(-204.37, 79.2) * mm});
            skLineSegment(sketch, "E239", {"start": v(-178.97, 3) * mm, "end": v(-178.97, 307.8) * mm, "construction": true});
            skLineSegment(sketch, "E240.MirrorCS", {"start": v(-204.37, 231.6) * mm, "end": v(-128.17, 231.6) * mm});
            skLineSegment(sketch, "E241.MirrorCS", {"start": v(-204.37, 307.8) * mm, "end": v(-204.37, 231.6) * mm});
            skPoint(sketch, "E242.orphan", {"position": v(-128.17, 307.8) * mm});
            skPoint(sketch, "E243.orphan", {"position": v(-128.17, 3) * mm});
            skLineSegment(sketch, "E244.bottom", {"start": v(-128.17, 218.9) * mm, "end": v(-122.84, 218.9) * mm});
            skLineSegment(sketch, "E244.top", {"start": v(-128.17, 193.5) * mm, "end": v(-122.84, 193.5) * mm});
            skLineSegment(sketch, "E244.right", {"start": v(-122.84, 218.9) * mm, "end": v(-122.84, 193.5) * mm});
            skLineSegment(sketch, "E245.trimOffspring", {"start": v(-128.17, 193.5) * mm, "end": v(-128.17, 168.1) * mm});
            skLineSegment(sketch, "E246.0.1.0", {"start": v(-128.17, 142.7) * mm, "end": v(-122.84, 142.7) * mm});
            skLineSegment(sketch, "E246.0.1.1", {"start": v(-122.84, 168.1) * mm, "end": v(-122.84, 142.7) * mm});
            skLineSegment(sketch, "E246.0.1.2", {"start": v(-128.17, 168.1) * mm, "end": v(-122.84, 168.1) * mm});
            skLineSegment(sketch, "E246.0.2.0", {"start": v(-128.17, 91.9) * mm, "end": v(-122.84, 91.9) * mm});
            skLineSegment(sketch, "E246.0.2.1", {"start": v(-122.84, 117.3) * mm, "end": v(-122.84, 91.9) * mm});
            skLineSegment(sketch, "E246.0.2.2", {"start": v(-128.17, 117.3) * mm, "end": v(-122.84, 117.3) * mm});
            skLineSegment(sketch, "E246.direction2", {"start": v(-128.17, 193.5) * mm, "end": v(-128.17, 168.1) * mm, "construction": true});
            skLineSegment(sketch, "E247.trimOffspring", {"start": v(-128.17, 142.7) * mm, "end": v(-128.17, 117.3) * mm});
            skLineSegment(sketch, "E248.trimOffspring", {"start": v(-128.17, 91.9) * mm, "end": v(-128.17, 79.2) * mm});
            skLineSegment(sketch, "E249.top", {"start": v(-229.77, 8.33) * mm, "end": v(-217.07, 8.33) * mm});
            skLineSegment(sketch, "E249.right", {"start": v(-217.07, 3) * mm, "end": v(-217.07, 8.33) * mm});
            skPoint(sketch, "E249.left.start.orphan", {"position": v(-229.77, 3) * mm});
            skLineSegment(sketch, "E250", {"start": v(-122.84, 155.4) * mm, "end": v(-232.07, 155.4) * mm, "construction": true});
            skLineSegment(sketch, "E251.MirrorCS", {"start": v(-229.77, 302.46) * mm, "end": v(-217.07, 302.46) * mm});
            skLineSegment(sketch, "E252.MirrorCS", {"start": v(-217.07, 307.8) * mm, "end": v(-217.07, 302.46) * mm});
            skPoint(sketch, "E253.orphan", {"position": v(-229.77, 307.8) * mm});
            skLineSegment(sketch, "E254.bottom", {"start": v(-229.77, 15.7) * mm, "end": v(-235.1, 15.7) * mm});
            skLineSegment(sketch, "E254.top", {"start": v(-229.77, 41.1) * mm, "end": v(-235.1, 41.1) * mm});
            skLineSegment(sketch, "E254.right", {"start": v(-235.1, 15.7) * mm, "end": v(-235.1, 41.1) * mm});
            skLineSegment(sketch, "E255.trimOffspring", {"start": v(-229.77, 15.7) * mm, "end": v(-229.77, 8.33) * mm});
            skLineSegment(sketch, "E256.0.1.0", {"start": v(-235.1, 66.5) * mm, "end": v(-235.1, 91.9) * mm});
            skLineSegment(sketch, "E256.0.1.1", {"start": v(-229.77, 91.9) * mm, "end": v(-235.1, 91.9) * mm});
            skLineSegment(sketch, "E256.0.1.2", {"start": v(-229.77, 66.5) * mm, "end": v(-235.1, 66.5) * mm});
            skLineSegment(sketch, "E256.0.2.0", {"start": v(-235.1, 117.3) * mm, "end": v(-235.1, 142.7) * mm});
            skLineSegment(sketch, "E256.0.2.1", {"start": v(-229.77, 142.7) * mm, "end": v(-235.1, 142.7) * mm});
            skLineSegment(sketch, "E256.0.2.2", {"start": v(-229.77, 117.3) * mm, "end": v(-235.1, 117.3) * mm});
            skLineSegment(sketch, "E256.0.3.0", {"start": v(-235.1, 168.1) * mm, "end": v(-235.1, 193.5) * mm});
            skLineSegment(sketch, "E256.0.3.1", {"start": v(-229.77, 193.5) * mm, "end": v(-235.1, 193.5) * mm});
            skLineSegment(sketch, "E256.0.3.2", {"start": v(-229.77, 168.1) * mm, "end": v(-235.1, 168.1) * mm});
            skLineSegment(sketch, "E256.0.4.0", {"start": v(-235.1, 218.9) * mm, "end": v(-235.1, 244.3) * mm});
            skLineSegment(sketch, "E256.0.4.1", {"start": v(-229.77, 244.3) * mm, "end": v(-235.1, 244.3) * mm});
            skLineSegment(sketch, "E256.0.4.2", {"start": v(-229.77, 218.9) * mm, "end": v(-235.1, 218.9) * mm});
            skLineSegment(sketch, "E256.0.5.0", {"start": v(-235.1, 269.7) * mm, "end": v(-235.1, 295.1) * mm});
            skLineSegment(sketch, "E256.0.5.1", {"start": v(-229.77, 295.1) * mm, "end": v(-235.1, 295.1) * mm});
            skLineSegment(sketch, "E256.0.5.2", {"start": v(-229.77, 269.7) * mm, "end": v(-235.1, 269.7) * mm});
            skLineSegment(sketch, "E256.direction1", {"start": v(-235.1, 15.7) * mm, "end": v(-210.1, 15.7) * mm, "construction": true});
            skLineSegment(sketch, "E256.direction2", {"start": v(-235.1, 15.7) * mm, "end": v(-235.1, 66.5) * mm, "construction": true});
            skLineSegment(sketch, "E257.bottom", {"start": v(-204.37, 87.45) * mm, "end": v(-153.57, 87.45) * mm});
            skLineSegment(sketch, "E257.top", {"start": v(-204.37, 82.37) * mm, "end": v(-153.57, 82.37) * mm});
            skLineSegment(sketch, "E257.left", {"start": v(-204.37, 87.45) * mm, "end": v(-204.37, 82.37) * mm});
            skLineSegment(sketch, "E257.right", {"start": v(-153.57, 87.45) * mm, "end": v(-153.57, 82.37) * mm});
            skLineSegment(sketch, "E258.MirrorCS", {"start": v(-204.37, 223.34) * mm, "end": v(-153.57, 223.34) * mm});
            skLineSegment(sketch, "E259.MirrorCS", {"start": v(-204.37, 223.34) * mm, "end": v(-204.37, 228.42) * mm});
            skLineSegment(sketch, "E260.MirrorCS", {"start": v(-153.57, 223.34) * mm, "end": v(-153.57, 228.42) * mm});
            skLineSegment(sketch, "E261.MirrorCS", {"start": v(-204.37, 228.42) * mm, "end": v(-153.57, 228.42) * mm});
            skLineSegment(sketch, "E262.trimOffspring", {"start": v(-229.77, 269.7) * mm, "end": v(-229.77, 244.3) * mm});
            skLineSegment(sketch, "E263.trimOffspring", {"start": v(-229.77, 218.9) * mm, "end": v(-229.77, 193.5) * mm});
            skLineSegment(sketch, "E264.trimOffspring", {"start": v(-229.77, 168.1) * mm, "end": v(-229.77, 142.7) * mm});
            skLineSegment(sketch, "E265.trimOffspring", {"start": v(-229.77, 117.3) * mm, "end": v(-229.77, 91.9) * mm});
            skLineSegment(sketch, "E266.trimOffspring", {"start": v(-229.77, 66.5) * mm, "end": v(-229.77, 41.1) * mm});
            skCircle(sketch, "E267", {"center": v(-178.97, 168.9) * mm, "radius": 8 * mm});
            skCircle(sketch, "E268.MirrorC", {"center": v(-178.97, 141.9) * mm, "radius": 8 * mm});
            skSolve(sketch);
        }
        {
            var Q0;
            Q0=makeQuery(id+"F5.imprint","IMPRINT",FACE,{"disambiguationData":[TD([[makeQuery(id+"F5.imprint","IMPRINT",EDGE,{"derivedFrom":sQuery(id+"F5.wireOp",EDGE,"E237.bottom")}),-1.0]])]});
            extrude(context, id + "F6", {"entities" : qUnion([Q0]), "depth" : getVariable(context, 'T0'), "offsetDistance" : 25 * mm});
        }
        {
            var Q0;
            Q0=qCreatedBy(makeId("Top.planeOp"),FACE);
            var sketch = newSketch(context, id + "F7", { "sketchPlane" : qUnion([Q0])});
            skArc(sketch, "E269", {"start": v(-262.46, -176.37) * mm, "mid": v(-267.65, -152.5) * mm, "end": v(-272.84, -176.37) * mm});
            skCircle(sketch, "E270", {"center": v(-283.15, -158) * mm, "radius": 1.7 * mm});
            skLineSegment(sketch, "E271.bottom", {"start": v(-280.35, -176.37) * mm, "end": v(-274, -176.37) * mm});
            skLineSegment(sketch, "E271.top", {"start": v(-280.35, -74.77) * mm, "end": v(-274, -74.77) * mm});
            skPoint(sketch, "E272.middle", {"position": v(-267.65, -153.63) * mm});
            skCircle(sketch, "E273.MirrorC", {"center": v(-252.15, -158) * mm, "radius": 1.7 * mm});
            skLineSegment(sketch, "E274.trimOffspring", {"start": v(-261.3, -176.37) * mm, "end": v(-254.95, -176.37) * mm});
            skPoint(sketch, "E275.middle", {"position": v(-267.65, -72.1) * mm});
            skLineSegment(sketch, "E276.trimOffspring", {"start": v(-261.3, -74.77) * mm, "end": v(-254.95, -74.77) * mm});
            skLineSegment(sketch, "E277.top", {"start": v(-293.05, -181.7) * mm, "end": v(-280.35, -181.7) * mm});
            skLineSegment(sketch, "E277.left", {"start": v(-293.05, -176.37) * mm, "end": v(-293.05, -181.7) * mm});
            skLineSegment(sketch, "E277.right", {"start": v(-280.35, -176.37) * mm, "end": v(-280.35, -181.7) * mm});
            skLineSegment(sketch, "E278.MirrorCS", {"start": v(-254.95, -176.37) * mm, "end": v(-254.95, -181.7) * mm});
            skLineSegment(sketch, "E279.MirrorCS", {"start": v(-242.25, -181.7) * mm, "end": v(-254.95, -181.7) * mm});
            skLineSegment(sketch, "E280.MirrorCS", {"start": v(-242.25, -176.37) * mm, "end": v(-242.25, -181.7) * mm});
            skLineSegment(sketch, "E281", {"start": v(-293.05, -125.57) * mm, "end": v(-242.25, -125.57) * mm, "construction": true});
            skLineSegment(sketch, "E282", {"start": v(-274, -176.37) * mm, "end": v(-272.84, -176.37) * mm});
            skPoint(sketch, "E272.top.end.orphan", {"position": v(-274, -130.9) * mm});
            skPoint(sketch, "E272.left.end.orphan", {"position": v(-261.3, -130.9) * mm});
            skLineSegment(sketch, "E283.MirrorCS", {"start": v(-293.05, -69.43) * mm, "end": v(-280.35, -69.43) * mm});
            skLineSegment(sketch, "E284.MirrorCS", {"start": v(-280.35, -74.77) * mm, "end": v(-280.35, -69.43) * mm});
            skLineSegment(sketch, "E285.MirrorCS", {"start": v(-293.05, -74.77) * mm, "end": v(-293.05, -69.43) * mm});
            skLineSegment(sketch, "E286.MirrorCS", {"start": v(-254.95, -74.77) * mm, "end": v(-254.95, -69.43) * mm});
            skLineSegment(sketch, "E287.MirrorCS", {"start": v(-242.25, -69.43) * mm, "end": v(-254.95, -69.43) * mm});
            skLineSegment(sketch, "E288.MirrorCS", {"start": v(-242.25, -74.77) * mm, "end": v(-242.25, -69.43) * mm});
            skLineSegment(sketch, "E289", {"start": v(-274, -74.77) * mm, "end": v(-261.3, -74.77) * mm});
            skPoint(sketch, "E275.right.end.orphan", {"position": v(-274, -69.43) * mm});
            skPoint(sketch, "E275.left.end.orphan", {"position": v(-261.3, -69.43) * mm});
            skLineSegment(sketch, "E290.bottom", {"start": v(-242.25, -176.37) * mm, "end": v(-209.48, -176.37) * mm});
            skLineSegment(sketch, "E290.top", {"start": v(-242.25, -74.77) * mm, "end": v(-209.48, -74.77) * mm});
            skPoint(sketch, "E291.orphan", {"position": v(-242.25, -74.77) * mm});
            skLineSegment(sketch, "E292.MirrorCS", {"start": v(-318.45, -150.97) * mm, "end": v(-318.45, -100.17) * mm});
            skLineSegment(sketch, "E293.MirrorCS", {"start": v(-293.05, -176.37) * mm, "end": v(-313.12, -176.37) * mm});
            skLineSegment(sketch, "E294.MirrorCS", {"start": v(-293.05, -74.77) * mm, "end": v(-313.12, -74.77) * mm});
            skPoint(sketch, "E295.orphan", {"position": v(-293.05, -74.77) * mm});
            skLineSegment(sketch, "E296.top", {"start": v(-318.45, -100.17) * mm, "end": v(-313.12, -100.17) * mm});
            skLineSegment(sketch, "E296.right", {"start": v(-313.12, -74.77) * mm, "end": v(-313.12, -100.17) * mm});
            skLineSegment(sketch, "E297.MirrorCS", {"start": v(-313.12, -176.37) * mm, "end": v(-313.12, -150.97) * mm});
            skLineSegment(sketch, "E298.MirrorCS", {"start": v(-318.45, -150.97) * mm, "end": v(-313.12, -150.97) * mm});
            skPoint(sketch, "E296.left.start.orphan", {"position": v(-318.45, -74.77) * mm});
            skPoint(sketch, "E299.orphan", {"position": v(-318.45, -176.37) * mm});
            skPoint(sketch, "E300.orphan", {"position": v(-204.15, -74.77) * mm});
            skPoint(sketch, "E301.orphan", {"position": v(-204.15, -176.37) * mm});
            skLineSegment(sketch, "E302.bottom", {"start": v(-209.48, -74.77) * mm, "end": v(-204.15, -74.77) * mm});
            skLineSegment(sketch, "E302.top", {"start": v(-222.18, -176.37) * mm, "end": v(-204.15, -176.37) * mm});
            skLineSegment(sketch, "E302.right", {"start": v(-204.15, -74.77) * mm, "end": v(-204.15, -100.17) * mm});
            skPoint(sketch, "E303.MirrorCS.end.orphan", {"position": v(-209.48, -100.17) * mm});
            skPoint(sketch, "E302.left.start.orphan", {"position": v(-209.48, -150.97) * mm});
            skLineSegment(sketch, "E304.bottom", {"start": v(-204.15, -100.17) * mm, "end": v(-198.82, -100.17) * mm});
            skLineSegment(sketch, "E304.top", {"start": v(-204.15, -150.97) * mm, "end": v(-198.82, -150.97) * mm});
            skLineSegment(sketch, "E304.right", {"start": v(-198.82, -100.17) * mm, "end": v(-198.82, -150.97) * mm});
            skLineSegment(sketch, "E305.trimOffspring", {"start": v(-204.15, -150.97) * mm, "end": v(-204.15, -176.37) * mm});
            skPoint(sketch, "E290.right.start.orphan", {"position": v(-204.15, -150.97) * mm});
            skLineSegment(sketch, "E306", {"start": v(-267.65, -74.77) * mm, "end": v(-267.65, -176.37) * mm, "construction": true});
            skLineSegment(sketch, "E307.right", {"start": v(-169.23, -74.77) * mm, "end": v(-169.23, -100.23) * mm});
            skLineSegment(sketch, "E308.bottom", {"start": v(-169.23, -151.03) * mm, "end": v(-163.9, -151.03) * mm});
            skLineSegment(sketch, "E308.top", {"start": v(-169.23, -100.23) * mm, "end": v(-163.9, -100.23) * mm});
            skLineSegment(sketch, "E308.right", {"start": v(-163.9, -151.03) * mm, "end": v(-163.9, -100.23) * mm});
            skLineSegment(sketch, "E309.trimOffspring", {"start": v(-169.23, -151.03) * mm, "end": v(-169.23, -176.37) * mm});
            skLineSegment(sketch, "E310.1.0.1", {"start": v(-97.22, -176.37) * mm, "end": v(-89.85, -176.37) * mm});
            skLineSegment(sketch, "E310.1.0.2", {"start": v(-89.85, -74.77) * mm, "end": v(-89.85, -100.23) * mm});
            skLineSegment(sketch, "E310.1.0.3", {"start": v(-97.22, -74.77) * mm, "end": v(-89.85, -74.77) * mm});
            skLineSegment(sketch, "E310.1.0.5", {"start": v(-122.62, -181.7) * mm, "end": v(-97.22, -181.7) * mm});
            skLineSegment(sketch, "E310.1.0.6", {"start": v(-122.62, -69.43) * mm, "end": v(-97.22, -69.43) * mm});
            skLineSegment(sketch, "E310.1.0.7", {"start": v(-109.92, -69.43) * mm, "end": v(-109.92, -181.7) * mm, "construction": true});
            skLineSegment(sketch, "E310.1.0.8", {"start": v(-84.52, -151.03) * mm, "end": v(-84.52, -100.23) * mm});
            skLineSegment(sketch, "E310.1.0.9", {"start": v(-89.85, -151.03) * mm, "end": v(-89.85, -176.37) * mm});
            skLineSegment(sketch, "E310.1.0.10", {"start": v(-97.22, -176.37) * mm, "end": v(-97.22, -181.7) * mm});
            skLineSegment(sketch, "E310.1.0.11", {"start": v(-97.22, -74.77) * mm, "end": v(-97.22, -69.43) * mm});
            skLineSegment(sketch, "E310.1.0.12", {"start": v(-89.85, -151.03) * mm, "end": v(-84.52, -151.03) * mm});
            skLineSegment(sketch, "E310.1.0.13", {"start": v(-122.62, -74.77) * mm, "end": v(-122.62, -69.43) * mm});
            skLineSegment(sketch, "E310.1.0.14", {"start": v(-122.62, -176.37) * mm, "end": v(-122.62, -181.7) * mm});
            skLineSegment(sketch, "E310.1.0.15", {"start": v(-89.85, -100.23) * mm, "end": v(-84.52, -100.23) * mm});
            skLineSegment(sketch, "E311", {"start": v(-169.23, -176.37) * mm, "end": v(-122.62, -176.37) * mm});
            skLineSegment(sketch, "E312", {"start": v(-169.23, -74.77) * mm, "end": v(-122.62, -74.77) * mm});
            skLineSegment(sketch, "E313.bottom", {"start": v(-592, -138) * mm, "end": v(-585.65, -138) * mm});
            skLineSegment(sketch, "E314.trimOffspring", {"start": v(-572.95, -138) * mm, "end": v(-566.6, -138) * mm});
            skLineSegment(sketch, "E315.top", {"start": v(-604.7, -143.34) * mm, "end": v(-592, -143.34) * mm});
            skLineSegment(sketch, "E315.left", {"start": v(-604.7, -138) * mm, "end": v(-604.7, -143.34) * mm});
            skLineSegment(sketch, "E315.right", {"start": v(-592, -138) * mm, "end": v(-592, -143.34) * mm});
            skLineSegment(sketch, "E316", {"start": v(-585.65, -138) * mm, "end": v(-572.95, -138) * mm});
            skPoint(sketch, "E317.orphan", {"position": v(-610.93, -138) * mm});
            skLineSegment(sketch, "E318.bottom", {"start": v(-611.05, -138) * mm, "end": v(-604.7, -138) * mm});
            skLineSegment(sketch, "E318.top", {"start": v(-591.05, -87.2) * mm, "end": v(-567.55, -87.2) * mm});
            skLineSegment(sketch, "E318.left", {"start": v(-611.05, -138) * mm, "end": v(-611.05, -107.2) * mm});
            skLineSegment(sketch, "E318.right", {"start": v(-547.55, -138) * mm, "end": v(-547.55, -107.2) * mm});
            skLineSegment(sketch, "E319.trimOffspring", {"start": v(-592, -138) * mm, "end": v(-566.6, -138) * mm});
            skLineSegment(sketch, "E320", {"start": v(-579.3, -87.2) * mm, "end": v(-579.3, -138) * mm, "construction": true});
            skLineSegment(sketch, "E321.MirrorCS", {"start": v(-566.6, -138) * mm, "end": v(-566.6, -143.34) * mm});
            skLineSegment(sketch, "E322.MirrorCS", {"start": v(-553.9, -143.34) * mm, "end": v(-566.6, -143.34) * mm});
            skLineSegment(sketch, "E323.MirrorCS", {"start": v(-553.9, -138) * mm, "end": v(-553.9, -143.34) * mm});
            skLineSegment(sketch, "E324.trimOffspring", {"start": v(-553.9, -138) * mm, "end": v(-547.55, -138) * mm});
            skPoint(sketch, "E325.visualSharp", {"position": v(-611.05, -87.2) * mm});
            skArc(sketch, "E325.filletArc", {"start": v(-591.05, -87.2) * mm, "mid": v(-605.2, -93.06) * mm, "end": v(-611.05, -107.2) * mm});
            skPoint(sketch, "E326.visualSharp", {"position": v(-547.55, -87.2) * mm});
            skArc(sketch, "E326.filletArc", {"start": v(-547.55, -107.2) * mm, "mid": v(-553.4, -93.06) * mm, "end": v(-567.55, -87.2) * mm});
            skCircle(sketch, "E327", {"center": v(-579.3, -119.5) * mm, "radius": 17 * mm});
            skLineSegment(sketch, "E328.trimOffspring", {"start": v(-262.46, -176.37) * mm, "end": v(-261.3, -176.37) * mm});
            skSolve(sketch);
        }
        {
            var Q0;
            Q0=makeQuery(id+"F7.imprint","IMPRINT",FACE,{"disambiguationData":[TD([[makeQuery(id+"F7.imprint","IMPRINT",EDGE,{"derivedFrom":sQuery(id+"F7.wireOp",EDGE,"E269")}),-1.0]])]});
            var Q1;
            Q1=makeQuery(id+"F7.imprint","IMPRINT",FACE,{"disambiguationData":[TD([[makeQuery(id+"F7.imprint","IMPRINT",EDGE,{"derivedFrom":sQuery(id+"F7.wireOp",EDGE,"E307.right")}),1.0]])]});
            var Q2;
            Q2=makeQuery(id+"F7.imprint","IMPRINT",FACE,{"disambiguationData":[TD([[makeQuery(id+"F7.imprint","IMPRINT",EDGE,{"derivedFrom":sQuery(id+"F7.wireOp",EDGE,"E315.top")}),1.0]])]});
            extrude(context, id + "F8", {"entities" : qUnion([Q0, Q1, Q2]), "depth" : getVariable(context, 'T0'), "offsetDistance" : 25 * mm});
        }
        {
            var Q0;
            Q0=qCreatedBy(makeId("Top.planeOp"),FACE);
            var sketch = newSketch(context, id + "F9", { "sketchPlane" : qUnion([Q0])});
            skLineSegment(sketch, "E329.left", {"start": v(630.12, 59.77) * mm, "end": v(630.12, 47.07) * mm});
            skLineSegment(sketch, "E329.right", {"start": v(1087.32, 59.77) * mm, "end": v(1087.32, 47.07) * mm});
            skLineSegment(sketch, "E330", {"start": v(630.12, -41.83) * mm, "end": v(1087.32, -41.83) * mm, "construction": true});
            skLineSegment(sketch, "E331", {"start": v(858.72, 110.57) * mm, "end": v(858.72, -194.23) * mm, "construction": true});
            skPoint(sketch, "E332.orphan", {"position": v(630.12, 110.57) * mm});
            skLineSegment(sketch, "E333.MirrorCS", {"start": v(973.02, -194.23) * mm, "end": v(973.02, -188.9) * mm});
            skPoint(sketch, "E334.orphan", {"position": v(630.12, -194.23) * mm});
            skPoint(sketch, "E335.orphan", {"position": v(1087.32, -194.23) * mm});
            skPoint(sketch, "E336.orphan", {"position": v(1087.32, 110.57) * mm});
            skLineSegment(sketch, "E337.bottom", {"start": v(1011.12, 31.2) * mm, "end": v(1023.82, 31.2) * mm});
            skLineSegment(sketch, "E337.top", {"start": v(1011.12, 25.86) * mm, "end": v(1023.82, 25.86) * mm});
            skLineSegment(sketch, "E337.left", {"start": v(1011.12, 31.2) * mm, "end": v(1011.12, 25.86) * mm});
            skLineSegment(sketch, "E337.right", {"start": v(1061.92, 31.2) * mm, "end": v(1061.92, 25.86) * mm});
            skLineSegment(sketch, "E338", {"start": v(1023.82, 31.2) * mm, "end": v(1023.82, 25.86) * mm});
            skLineSegment(sketch, "E339", {"start": v(1049.22, 31.2) * mm, "end": v(1049.22, 25.86) * mm});
            skLineSegment(sketch, "E340.trimOffspring", {"start": v(1049.22, 31.2) * mm, "end": v(1061.92, 31.2) * mm});
            skLineSegment(sketch, "E341.trimOffspring", {"start": v(1049.22, 25.86) * mm, "end": v(1061.92, 25.86) * mm});
            skLineSegment(sketch, "E342.MirrorCS", {"start": v(1049.22, -114.86) * mm, "end": v(1049.22, -109.52) * mm});
            skLineSegment(sketch, "E343.MirrorCS", {"start": v(1011.12, -114.86) * mm, "end": v(1011.12, -109.52) * mm});
            skLineSegment(sketch, "E344.MirrorCS", {"start": v(1061.92, -114.86) * mm, "end": v(1061.92, -109.52) * mm});
            skLineSegment(sketch, "E345.MirrorCS", {"start": v(1023.82, -114.86) * mm, "end": v(1023.82, -109.52) * mm});
            skLineSegment(sketch, "E346.MirrorCS", {"start": v(1049.22, -114.86) * mm, "end": v(1061.92, -114.86) * mm});
            skLineSegment(sketch, "E347.MirrorCS", {"start": v(1011.12, -114.86) * mm, "end": v(1023.82, -114.86) * mm});
            skLineSegment(sketch, "E348.MirrorCS", {"start": v(1049.22, -109.52) * mm, "end": v(1061.92, -109.52) * mm});
            skLineSegment(sketch, "E349.MirrorCS", {"start": v(1011.12, -109.52) * mm, "end": v(1023.82, -109.52) * mm});
            skLineSegment(sketch, "E350.MirrorCS", {"start": v(706.32, 31.2) * mm, "end": v(706.32, 25.86) * mm});
            skLineSegment(sketch, "E351.MirrorCS", {"start": v(668.22, 31.2) * mm, "end": v(668.22, 25.86) * mm});
            skLineSegment(sketch, "E352.MirrorCS", {"start": v(655.52, 31.2) * mm, "end": v(655.52, 25.86) * mm});
            skLineSegment(sketch, "E353.MirrorCS", {"start": v(706.32, 25.86) * mm, "end": v(693.62, 25.86) * mm});
            skLineSegment(sketch, "E354.MirrorCS", {"start": v(693.62, 31.2) * mm, "end": v(693.62, 25.86) * mm});
            skLineSegment(sketch, "E355.MirrorCS", {"start": v(706.32, 31.2) * mm, "end": v(693.62, 31.2) * mm});
            skLineSegment(sketch, "E356.MirrorCS", {"start": v(668.22, 25.86) * mm, "end": v(655.52, 25.86) * mm});
            skLineSegment(sketch, "E357.MirrorCS", {"start": v(668.22, 31.2) * mm, "end": v(655.52, 31.2) * mm});
            skLineSegment(sketch, "E358.MirrorCS", {"start": v(706.32, -114.86) * mm, "end": v(706.32, -109.52) * mm});
            skLineSegment(sketch, "E359.MirrorCS", {"start": v(668.22, -114.86) * mm, "end": v(668.22, -109.52) * mm});
            skLineSegment(sketch, "E360.MirrorCS", {"start": v(655.52, -114.86) * mm, "end": v(655.52, -109.52) * mm});
            skLineSegment(sketch, "E361.MirrorCS", {"start": v(668.22, -114.86) * mm, "end": v(655.52, -114.86) * mm});
            skLineSegment(sketch, "E362.MirrorCS", {"start": v(668.22, -109.52) * mm, "end": v(655.52, -109.52) * mm});
            skLineSegment(sketch, "E363.MirrorCS", {"start": v(693.62, -114.86) * mm, "end": v(693.62, -109.52) * mm});
            skLineSegment(sketch, "E364.MirrorCS", {"start": v(706.32, -114.86) * mm, "end": v(693.62, -114.86) * mm});
            skLineSegment(sketch, "E365.MirrorCS", {"start": v(706.32, -109.52) * mm, "end": v(693.62, -109.52) * mm});
            skLineSegment(sketch, "E366.trimOffspring", {"start": v(630.12, -130.73) * mm, "end": v(630.12, -143.43) * mm});
            skLineSegment(sketch, "E367.trimOffspring", {"start": v(1087.32, -130.73) * mm, "end": v(1087.32, -143.43) * mm});
            skPoint(sketch, "E368.trimOffspring.start.orphan", {"position": v(998.42, 110.57) * mm});
            skLineSegment(sketch, "E369.bottom", {"start": v(744.42, -156.13) * mm, "end": v(749.76, -156.13) * mm});
            skLineSegment(sketch, "E369.top", {"start": v(744.42, -181.53) * mm, "end": v(749.76, -181.53) * mm});
            skLineSegment(sketch, "E369.right", {"start": v(749.76, -156.13) * mm, "end": v(749.76, -181.53) * mm});
            skLineSegment(sketch, "E370.MirrorCS", {"start": v(744.42, 97.87) * mm, "end": v(749.76, 97.87) * mm});
            skLineSegment(sketch, "E371.MirrorCS", {"start": v(744.42, 72.47) * mm, "end": v(749.76, 72.47) * mm});
            skLineSegment(sketch, "E372.MirrorCS", {"start": v(749.76, 72.47) * mm, "end": v(749.76, 97.87) * mm});
            skLineSegment(sketch, "E373.MirrorCS", {"start": v(973.02, 97.87) * mm, "end": v(967.69, 97.87) * mm});
            skLineSegment(sketch, "E374.MirrorCS", {"start": v(967.69, 72.47) * mm, "end": v(967.69, 97.87) * mm});
            skLineSegment(sketch, "E375.MirrorCS", {"start": v(973.02, 72.47) * mm, "end": v(967.69, 72.47) * mm});
            skLineSegment(sketch, "E376.MirrorCS", {"start": v(973.02, -156.13) * mm, "end": v(967.69, -156.13) * mm});
            skLineSegment(sketch, "E377.MirrorCS", {"start": v(967.69, -156.13) * mm, "end": v(967.69, -181.53) * mm});
            skLineSegment(sketch, "E378.MirrorCS", {"start": v(973.02, -181.53) * mm, "end": v(967.69, -181.53) * mm});
            skPoint(sketch, "E379.MirrorCS.start.orphan", {"position": v(998.42, -194.23) * mm});
            skLineSegment(sketch, "E380.bottom", {"start": v(630.12, 110.57) * mm, "end": v(642.82, 110.57) * mm});
            skLineSegment(sketch, "E380.top", {"start": v(630.12, -194.23) * mm, "end": v(642.82, -194.23) * mm});
            skLineSegment(sketch, "E380.left", {"start": v(630.12, 110.57) * mm, "end": v(630.12, 97.87) * mm});
            skLineSegment(sketch, "E380.right", {"start": v(1087.32, 110.57) * mm, "end": v(1087.32, 97.87) * mm});
            skPoint(sketch, "E381.trimOffspring.end.orphan", {"position": v(744.42, 59.77) * mm});
            skPoint(sketch, "E382.trimOffspring.end.orphan", {"position": v(744.42, -143.43) * mm});
            skPoint(sketch, "E383.trimOffspring.end.orphan", {"position": v(973.02, -143.43) * mm});
            skPoint(sketch, "E384.MirrorCS.start.orphan", {"position": v(973.02, 110.57) * mm});
            skPoint(sketch, "E385.trimOffspring.end.orphan", {"position": v(973.02, 59.77) * mm});
            skLineSegment(sketch, "E386", {"start": v(744.42, 97.87) * mm, "end": v(744.42, 72.47) * mm});
            skLineSegment(sketch, "E387", {"start": v(973.02, 97.87) * mm, "end": v(973.02, 72.47) * mm});
            skLineSegment(sketch, "E388", {"start": v(973.02, -156.13) * mm, "end": v(973.02, -181.53) * mm});
            skLineSegment(sketch, "E389", {"start": v(744.42, -156.13) * mm, "end": v(744.42, -181.53) * mm});
            skLineSegment(sketch, "E390.bottom", {"start": v(630.12, -181.53) * mm, "end": v(635.46, -181.53) * mm});
            skLineSegment(sketch, "E390.top", {"start": v(630.12, -156.13) * mm, "end": v(635.46, -156.13) * mm});
            skLineSegment(sketch, "E390.right", {"start": v(635.46, -181.53) * mm, "end": v(635.46, -156.13) * mm});
            skLineSegment(sketch, "E391.top", {"start": v(642.82, -188.9) * mm, "end": v(668.22, -188.9) * mm});
            skLineSegment(sketch, "E391.left", {"start": v(642.82, -194.23) * mm, "end": v(642.82, -188.9) * mm});
            skLineSegment(sketch, "E391.right", {"start": v(668.22, -194.23) * mm, "end": v(668.22, -188.9) * mm});
            skLineSegment(sketch, "E392.0.1.0", {"start": v(635.46, -130.73) * mm, "end": v(635.46, -105.33) * mm});
            skLineSegment(sketch, "E392.0.1.1", {"start": v(630.12, -130.73) * mm, "end": v(635.46, -130.73) * mm});
            skLineSegment(sketch, "E392.0.1.2", {"start": v(630.12, -105.33) * mm, "end": v(635.46, -105.33) * mm});
            skLineSegment(sketch, "E392.0.2.0", {"start": v(635.46, -79.93) * mm, "end": v(635.46, -54.53) * mm});
            skLineSegment(sketch, "E392.0.2.1", {"start": v(630.12, -79.93) * mm, "end": v(635.46, -79.93) * mm});
            skLineSegment(sketch, "E392.0.2.2", {"start": v(630.12, -54.53) * mm, "end": v(635.46, -54.53) * mm});
            skLineSegment(sketch, "E392.0.3.0", {"start": v(635.46, -29.13) * mm, "end": v(635.46, -3.73) * mm});
            skLineSegment(sketch, "E392.0.3.1", {"start": v(630.12, -29.13) * mm, "end": v(635.46, -29.13) * mm});
            skLineSegment(sketch, "E392.0.3.2", {"start": v(630.12, -3.73) * mm, "end": v(635.46, -3.73) * mm});
            skLineSegment(sketch, "E392.0.4.0", {"start": v(635.46, 21.67) * mm, "end": v(635.46, 47.07) * mm});
            skLineSegment(sketch, "E392.0.4.1", {"start": v(630.12, 21.67) * mm, "end": v(635.46, 21.67) * mm});
            skLineSegment(sketch, "E392.0.4.2", {"start": v(630.12, 47.07) * mm, "end": v(635.46, 47.07) * mm});
            skLineSegment(sketch, "E392.0.5.0", {"start": v(635.46, 72.47) * mm, "end": v(635.46, 97.87) * mm});
            skLineSegment(sketch, "E392.0.5.1", {"start": v(630.12, 72.47) * mm, "end": v(635.46, 72.47) * mm});
            skLineSegment(sketch, "E392.0.5.2", {"start": v(630.12, 97.87) * mm, "end": v(635.46, 97.87) * mm});
            skLineSegment(sketch, "E392.direction2", {"start": v(635.46, -181.53) * mm, "end": v(635.46, -130.73) * mm, "construction": true});
            skLineSegment(sketch, "E393.trimOffspring", {"start": v(630.12, 72.47) * mm, "end": v(630.12, 47.07) * mm});
            skLineSegment(sketch, "E394.trimOffspring", {"start": v(630.12, 21.67) * mm, "end": v(630.12, -3.73) * mm});
            skLineSegment(sketch, "E395.trimOffspring", {"start": v(630.12, -29.13) * mm, "end": v(630.12, -54.53) * mm});
            skPoint(sketch, "E396.orphan", {"position": v(630.12, 21.67) * mm});
            skLineSegment(sketch, "E397.trimOffspring", {"start": v(630.12, -79.93) * mm, "end": v(630.12, -105.33) * mm});
            skLineSegment(sketch, "E398.trimOffspring", {"start": v(630.12, -130.73) * mm, "end": v(630.12, -156.13) * mm});
            skPoint(sketch, "E399.orphan", {"position": v(630.12, -105.33) * mm});
            skLineSegment(sketch, "E400.trimOffspring", {"start": v(630.12, -181.53) * mm, "end": v(630.12, -194.23) * mm});
            skLineSegment(sketch, "E401.MirrorCS", {"start": v(1087.32, -130.73) * mm, "end": v(1081.99, -130.73) * mm});
            skLineSegment(sketch, "E402.MirrorCS", {"start": v(1087.32, -105.33) * mm, "end": v(1081.99, -105.33) * mm});
            skLineSegment(sketch, "E403.MirrorCS", {"start": v(1087.32, 97.87) * mm, "end": v(1081.99, 97.87) * mm});
            skLineSegment(sketch, "E404.MirrorCS", {"start": v(1087.32, -29.13) * mm, "end": v(1081.99, -29.13) * mm});
            skLineSegment(sketch, "E405.MirrorCS", {"start": v(1087.32, 72.47) * mm, "end": v(1081.99, 72.47) * mm});
            skLineSegment(sketch, "E406.MirrorCS", {"start": v(1087.32, -3.73) * mm, "end": v(1081.99, -3.73) * mm});
            skLineSegment(sketch, "E407.MirrorCS", {"start": v(1087.32, -79.93) * mm, "end": v(1081.99, -79.93) * mm});
            skLineSegment(sketch, "E408.MirrorCS", {"start": v(1087.32, -156.13) * mm, "end": v(1081.99, -156.13) * mm});
            skLineSegment(sketch, "E409.MirrorCS", {"start": v(1087.32, 21.67) * mm, "end": v(1081.99, 21.67) * mm});
            skLineSegment(sketch, "E410.MirrorCS", {"start": v(1087.32, 47.07) * mm, "end": v(1081.99, 47.07) * mm});
            skLineSegment(sketch, "E411.MirrorCS", {"start": v(1087.32, -181.53) * mm, "end": v(1081.99, -181.53) * mm});
            skLineSegment(sketch, "E412.MirrorCS", {"start": v(1087.32, -54.53) * mm, "end": v(1081.99, -54.53) * mm});
            skLineSegment(sketch, "E413.MirrorCS", {"start": v(1081.99, -181.53) * mm, "end": v(1081.99, -156.13) * mm});
            skLineSegment(sketch, "E414.MirrorCS", {"start": v(1081.99, 72.47) * mm, "end": v(1081.99, 97.87) * mm});
            skLineSegment(sketch, "E415.MirrorCS", {"start": v(1087.32, 21.67) * mm, "end": v(1087.32, -3.73) * mm});
            skLineSegment(sketch, "E416.MirrorCS", {"start": v(1081.99, -29.13) * mm, "end": v(1081.99, -3.73) * mm});
            skLineSegment(sketch, "E417.MirrorCS", {"start": v(1081.99, 21.67) * mm, "end": v(1081.99, 47.07) * mm});
            skLineSegment(sketch, "E418.MirrorCS", {"start": v(1087.32, -79.93) * mm, "end": v(1087.32, -105.33) * mm});
            skPoint(sketch, "E419.MirrorP", {"position": v(1087.32, -105.33) * mm});
            skLineSegment(sketch, "E420.MirrorCS", {"start": v(1087.32, -29.13) * mm, "end": v(1087.32, -54.53) * mm});
            skLineSegment(sketch, "E421.MirrorCS", {"start": v(1081.99, -79.93) * mm, "end": v(1081.99, -54.53) * mm});
            skLineSegment(sketch, "E422.MirrorCS", {"start": v(1087.32, -130.73) * mm, "end": v(1087.32, -156.13) * mm});
            skLineSegment(sketch, "E423.MirrorCS", {"start": v(1081.99, -130.73) * mm, "end": v(1081.99, -105.33) * mm});
            skPoint(sketch, "E424.MirrorP", {"position": v(1087.32, 21.67) * mm});
            skLineSegment(sketch, "E425.MirrorCS", {"start": v(1081.99, -181.53) * mm, "end": v(1081.99, -130.73) * mm, "construction": true});
            skLineSegment(sketch, "E426.MirrorCS", {"start": v(1087.32, -181.53) * mm, "end": v(1087.32, -194.23) * mm});
            skLineSegment(sketch, "E427.MirrorCS", {"start": v(1087.32, 72.47) * mm, "end": v(1087.32, 47.07) * mm});
            skLineSegment(sketch, "E428.1.0.0", {"start": v(693.62, -188.9) * mm, "end": v(719.02, -188.9) * mm});
            skLineSegment(sketch, "E428.1.0.1", {"start": v(693.62, -194.23) * mm, "end": v(693.62, -188.9) * mm});
            skLineSegment(sketch, "E428.1.0.2", {"start": v(719.02, -194.23) * mm, "end": v(719.02, -188.9) * mm});
            skLineSegment(sketch, "E428.2.0.0", {"start": v(744.42, -188.9) * mm, "end": v(769.82, -188.9) * mm});
            skLineSegment(sketch, "E428.2.0.1", {"start": v(744.42, -194.23) * mm, "end": v(744.42, -188.9) * mm});
            skLineSegment(sketch, "E428.2.0.2", {"start": v(769.82, -194.23) * mm, "end": v(769.82, -188.9) * mm});
            skLineSegment(sketch, "E428.3.0.0", {"start": v(795.22, -188.9) * mm, "end": v(820.62, -188.9) * mm});
            skLineSegment(sketch, "E428.3.0.1", {"start": v(795.22, -194.23) * mm, "end": v(795.22, -188.9) * mm});
            skLineSegment(sketch, "E428.3.0.2", {"start": v(820.62, -194.23) * mm, "end": v(820.62, -188.9) * mm});
            skLineSegment(sketch, "E428.4.0.0", {"start": v(846.02, -188.9) * mm, "end": v(871.42, -188.9) * mm});
            skLineSegment(sketch, "E428.4.0.1", {"start": v(846.02, -194.23) * mm, "end": v(846.02, -188.9) * mm});
            skLineSegment(sketch, "E428.4.0.2", {"start": v(871.42, -194.23) * mm, "end": v(871.42, -188.9) * mm});
            skLineSegment(sketch, "E428.5.0.0", {"start": v(896.82, -188.9) * mm, "end": v(922.22, -188.9) * mm});
            skLineSegment(sketch, "E428.5.0.1", {"start": v(896.82, -194.23) * mm, "end": v(896.82, -188.9) * mm});
            skLineSegment(sketch, "E428.5.0.2", {"start": v(922.22, -194.23) * mm, "end": v(922.22, -188.9) * mm});
            skLineSegment(sketch, "E428.6.0.0", {"start": v(947.62, -188.9) * mm, "end": v(973.02, -188.9) * mm});
            skLineSegment(sketch, "E428.6.0.1", {"start": v(947.62, -194.23) * mm, "end": v(947.62, -188.9) * mm});
            skLineSegment(sketch, "E428.7.0.0", {"start": v(998.42, -188.9) * mm, "end": v(1023.82, -188.9) * mm});
            skLineSegment(sketch, "E428.7.0.1", {"start": v(998.42, -194.23) * mm, "end": v(998.42, -188.9) * mm});
            skLineSegment(sketch, "E428.7.0.2", {"start": v(1023.82, -194.23) * mm, "end": v(1023.82, -188.9) * mm});
            skLineSegment(sketch, "E428.8.0.0", {"start": v(1049.22, -188.9) * mm, "end": v(1074.62, -188.9) * mm});
            skLineSegment(sketch, "E428.8.0.1", {"start": v(1049.22, -194.23) * mm, "end": v(1049.22, -188.9) * mm});
            skLineSegment(sketch, "E428.8.0.2", {"start": v(1074.62, -194.23) * mm, "end": v(1074.62, -188.9) * mm});
            skLineSegment(sketch, "E428.direction1", {"start": v(642.82, -188.9) * mm, "end": v(693.62, -188.9) * mm, "construction": true});
            skLineSegment(sketch, "E429.trimOffspring", {"start": v(668.22, -194.23) * mm, "end": v(693.62, -194.23) * mm});
            skLineSegment(sketch, "E430.trimOffspring", {"start": v(719.02, -194.23) * mm, "end": v(744.42, -194.23) * mm});
            skPoint(sketch, "E329.top.end.orphan", {"position": v(769.82, -194.23) * mm});
            skPoint(sketch, "E329.top.start.orphan", {"position": v(744.42, -194.23) * mm});
            skLineSegment(sketch, "E431.trimOffspring", {"start": v(820.62, -194.23) * mm, "end": v(846.02, -194.23) * mm});
            skLineSegment(sketch, "E432.trimOffspring", {"start": v(769.82, -194.23) * mm, "end": v(795.22, -194.23) * mm});
            skLineSegment(sketch, "E433.trimOffspring", {"start": v(871.42, -194.23) * mm, "end": v(896.82, -194.23) * mm});
            skLineSegment(sketch, "E434.trimOffspring", {"start": v(922.22, -194.23) * mm, "end": v(947.62, -194.23) * mm});
            skLineSegment(sketch, "E435.trimOffspring", {"start": v(973.02, -194.23) * mm, "end": v(998.42, -194.23) * mm});
            skLineSegment(sketch, "E436.trimOffspring", {"start": v(1023.82, -194.23) * mm, "end": v(1049.22, -194.23) * mm});
            skLineSegment(sketch, "E437.trimOffspring", {"start": v(1074.62, -194.23) * mm, "end": v(1087.32, -194.23) * mm});
            skLineSegment(sketch, "E438.MirrorCS", {"start": v(1087.32, 97.87) * mm, "end": v(1087.32, 110.57) * mm});
            skLineSegment(sketch, "E439.MirrorCS", {"start": v(973.02, 110.57) * mm, "end": v(973.02, 105.23) * mm});
            skLineSegment(sketch, "E440.MirrorCS", {"start": v(630.12, 97.87) * mm, "end": v(630.12, 110.57) * mm});
            skLineSegment(sketch, "E441.MirrorCS", {"start": v(642.82, 110.57) * mm, "end": v(642.82, 105.23) * mm});
            skLineSegment(sketch, "E442.MirrorCS", {"start": v(744.42, 110.57) * mm, "end": v(744.42, 105.23) * mm});
            skLineSegment(sketch, "E443.MirrorCS", {"start": v(769.82, 110.57) * mm, "end": v(769.82, 105.23) * mm});
            skLineSegment(sketch, "E444.MirrorCS", {"start": v(998.42, 110.57) * mm, "end": v(998.42, 105.23) * mm});
            skLineSegment(sketch, "E445.MirrorCS", {"start": v(693.62, 110.57) * mm, "end": v(693.62, 105.23) * mm});
            skLineSegment(sketch, "E446.MirrorCS", {"start": v(668.22, 110.57) * mm, "end": v(668.22, 105.23) * mm});
            skLineSegment(sketch, "E447.MirrorCS", {"start": v(820.62, 110.57) * mm, "end": v(820.62, 105.23) * mm});
            skLineSegment(sketch, "E448.MirrorCS", {"start": v(846.02, 110.57) * mm, "end": v(846.02, 105.23) * mm});
            skLineSegment(sketch, "E449.MirrorCS", {"start": v(642.82, 105.23) * mm, "end": v(668.22, 105.23) * mm});
            skLineSegment(sketch, "E450.MirrorCS", {"start": v(1074.62, 110.57) * mm, "end": v(1074.62, 105.23) * mm});
            skLineSegment(sketch, "E451.MirrorCS", {"start": v(719.02, 110.57) * mm, "end": v(719.02, 105.23) * mm});
            skLineSegment(sketch, "E452.MirrorCS", {"start": v(896.82, 110.57) * mm, "end": v(896.82, 105.23) * mm});
            skLineSegment(sketch, "E453.MirrorCS", {"start": v(922.22, 110.57) * mm, "end": v(922.22, 105.23) * mm});
            skLineSegment(sketch, "E454.MirrorCS", {"start": v(1049.22, 110.57) * mm, "end": v(1049.22, 105.23) * mm});
            skLineSegment(sketch, "E455.MirrorCS", {"start": v(1074.62, 110.57) * mm, "end": v(1087.32, 110.57) * mm});
            skLineSegment(sketch, "E456.MirrorCS", {"start": v(947.62, 110.57) * mm, "end": v(947.62, 105.23) * mm});
            skLineSegment(sketch, "E457.MirrorCS", {"start": v(1023.82, 110.57) * mm, "end": v(1023.82, 105.23) * mm});
            skLineSegment(sketch, "E458.MirrorCS", {"start": v(795.22, 110.57) * mm, "end": v(795.22, 105.23) * mm});
            skLineSegment(sketch, "E459.MirrorCS", {"start": v(871.42, 110.57) * mm, "end": v(871.42, 105.23) * mm});
            skLineSegment(sketch, "E460.MirrorCS", {"start": v(642.82, 105.23) * mm, "end": v(668.22, 105.23) * mm, "construction": true});
            skLineSegment(sketch, "E461.MirrorCS", {"start": v(668.22, 110.57) * mm, "end": v(693.62, 110.57) * mm});
            skLineSegment(sketch, "E462.MirrorCS", {"start": v(973.02, 110.57) * mm, "end": v(998.42, 110.57) * mm});
            skLineSegment(sketch, "E463.MirrorCS", {"start": v(947.62, 105.23) * mm, "end": v(973.02, 105.23) * mm});
            skLineSegment(sketch, "E464.MirrorCS", {"start": v(719.02, 110.57) * mm, "end": v(744.42, 110.57) * mm});
            skLineSegment(sketch, "E465.MirrorCS", {"start": v(1049.22, 105.23) * mm, "end": v(1074.62, 105.23) * mm});
            skLineSegment(sketch, "E466.MirrorCS", {"start": v(922.22, 110.57) * mm, "end": v(947.62, 110.57) * mm});
            skLineSegment(sketch, "E467.MirrorCS", {"start": v(693.62, 105.23) * mm, "end": v(719.02, 105.23) * mm});
            skLineSegment(sketch, "E468.MirrorCS", {"start": v(871.42, 110.57) * mm, "end": v(896.82, 110.57) * mm});
            skLineSegment(sketch, "E469.MirrorCS", {"start": v(769.82, 110.57) * mm, "end": v(795.22, 110.57) * mm});
            skLineSegment(sketch, "E470.MirrorCS", {"start": v(858.72, -194.23) * mm, "end": v(858.72, 110.57) * mm, "construction": true});
            skLineSegment(sketch, "E471.MirrorCS", {"start": v(896.82, 105.23) * mm, "end": v(922.22, 105.23) * mm});
            skLineSegment(sketch, "E472.MirrorCS", {"start": v(795.22, 105.23) * mm, "end": v(820.62, 105.23) * mm});
            skLineSegment(sketch, "E473.MirrorCS", {"start": v(1023.82, 110.57) * mm, "end": v(1049.22, 110.57) * mm});
            skLineSegment(sketch, "E474.MirrorCS", {"start": v(744.42, 105.23) * mm, "end": v(769.82, 105.23) * mm});
            skLineSegment(sketch, "E475.MirrorCS", {"start": v(846.02, 105.23) * mm, "end": v(871.42, 105.23) * mm});
            skLineSegment(sketch, "E476.MirrorCS", {"start": v(998.42, 105.23) * mm, "end": v(1023.82, 105.23) * mm});
            skLineSegment(sketch, "E477.MirrorCS", {"start": v(820.62, 110.57) * mm, "end": v(846.02, 110.57) * mm});
            skPoint(sketch, "E329.bottom.end.orphan", {"position": v(769.82, 110.57) * mm});
            skPoint(sketch, "E329.bottom.start.orphan", {"position": v(744.42, 110.57) * mm});
            skPoint(sketch, "E478.trimOffspring.start.orphan", {"position": v(947.62, 110.57) * mm});
            skLineSegment(sketch, "E479.bottom", {"start": v(655.52, 97.87) * mm, "end": v(668.22, 97.87) * mm});
            skLineSegment(sketch, "E479.top", {"start": v(655.52, 92.91) * mm, "end": v(668.22, 92.91) * mm});
            skLineSegment(sketch, "E479.left", {"start": v(655.52, 97.87) * mm, "end": v(655.52, 92.91) * mm});
            skLineSegment(sketch, "E479.right", {"start": v(668.22, 97.87) * mm, "end": v(668.22, 92.91) * mm});
            skLineSegment(sketch, "E480.bottom", {"start": v(642.82, 85.17) * mm, "end": v(647.78, 85.17) * mm});
            skLineSegment(sketch, "E480.top", {"start": v(642.82, 72.47) * mm, "end": v(647.78, 72.47) * mm});
            skLineSegment(sketch, "E480.left", {"start": v(642.82, 85.17) * mm, "end": v(642.82, 72.47) * mm});
            skLineSegment(sketch, "E480.right", {"start": v(647.78, 85.17) * mm, "end": v(647.78, 72.47) * mm});
            skLineSegment(sketch, "E481.1.0.0", {"start": v(949.99, -173.02) * mm, "end": v(962.69, -173.02) * mm});
            skLineSegment(sketch, "E481.1.0.1", {"start": v(950, -177.98) * mm, "end": v(949.99, -173.02) * mm});
            skLineSegment(sketch, "E481.1.0.2", {"start": v(950, -177.98) * mm, "end": v(962.69, -177.98) * mm});
            skLineSegment(sketch, "E481.1.0.3", {"start": v(962.69, -177.98) * mm, "end": v(962.69, -173.02) * mm});
            skLineSegment(sketch, "E482.0.1.0", {"start": v(642.82, -39.83) * mm, "end": v(647.78, -39.83) * mm});
            skLineSegment(sketch, "E482.0.1.1", {"start": v(647.78, -39.83) * mm, "end": v(647.78, -52.53) * mm});
            skLineSegment(sketch, "E482.0.1.2", {"start": v(642.82, -39.83) * mm, "end": v(642.82, -52.53) * mm});
            skLineSegment(sketch, "E482.0.1.3", {"start": v(642.82, -52.53) * mm, "end": v(647.78, -52.53) * mm});
            skLineSegment(sketch, "E482.direction1", {"start": v(642.82, 85.17) * mm, "end": v(667.82, 85.17) * mm, "construction": true});
            skLineSegment(sketch, "E482.direction2", {"start": v(642.82, 85.17) * mm, "end": v(642.82, -39.83) * mm, "construction": true});
            skCircle(sketch, "E483", {"center": v(655.52, -168.83) * mm, "radius": 12.7 * mm});
            skCircle(sketch, "E484.0.1.0", {"center": v(655.52, -79.93) * mm, "radius": 12.7 * mm});
            skLineSegment(sketch, "E484.direction1", {"start": v(655.52, -168.83) * mm, "end": v(680.52, -168.83) * mm, "construction": true});
            skLineSegment(sketch, "E484.direction2", {"start": v(655.52, -168.83) * mm, "end": v(655.52, -79.93) * mm, "construction": true});
            skLineSegment(sketch, "E485.1.0.0", {"start": v(690, -177.98) * mm, "end": v(689.99, -173.02) * mm});
            skLineSegment(sketch, "E485.1.0.1", {"start": v(690, -177.98) * mm, "end": v(702.69, -177.98) * mm});
            skLineSegment(sketch, "E485.1.0.2", {"start": v(702.69, -177.98) * mm, "end": v(702.69, -173.02) * mm});
            skLineSegment(sketch, "E485.1.0.3", {"start": v(689.99, -173.02) * mm, "end": v(702.69, -173.02) * mm});
            skLineSegment(sketch, "E485.direction1", {"start": v(950, -177.98) * mm, "end": v(690, -177.98) * mm, "construction": true});
            skCircle(sketch, "E486.1.0", {"center": v(1061.92, -3.73) * mm, "radius": 12.7 * mm});
            skCircle(sketch, "E486.1.1", {"center": v(1061.92, 85.17) * mm, "radius": 12.7 * mm});
            skPoint(sketch, "E486.center", {"position": v(858.72, -41.83) * mm});
            skLineSegment(sketch, "E487.1.0.0", {"start": v(1020.52, 97.87) * mm, "end": v(1033.22, 97.87) * mm});
            skLineSegment(sketch, "E487.1.0.1", {"start": v(1020.52, 92.91) * mm, "end": v(1033.22, 92.91) * mm});
            skLineSegment(sketch, "E487.1.0.2", {"start": v(1020.52, 97.87) * mm, "end": v(1020.52, 92.91) * mm});
            skLineSegment(sketch, "E487.1.0.3", {"start": v(1033.22, 97.87) * mm, "end": v(1033.22, 92.91) * mm});
            skLineSegment(sketch, "E487.direction1", {"start": v(655.52, 92.91) * mm, "end": v(1020.52, 92.91) * mm, "construction": true});
            skCircle(sketch, "E488", {"center": v(1062.59, -175.18) * mm, "radius": 2.16 * mm});
            skCircle(sketch, "E489.0.1.0", {"center": v(1062.59, -105.33) * mm, "radius": 2.16 * mm});
            skCircle(sketch, "E489.1.0.0", {"center": v(992.74, -175.18) * mm, "radius": 2.16 * mm});
            skCircle(sketch, "E489.1.1.0", {"center": v(992.74, -105.33) * mm, "radius": 2.16 * mm});
            skLineSegment(sketch, "E489.direction1", {"start": v(1062.59, -175.18) * mm, "end": v(992.74, -175.18) * mm, "construction": true});
            skLineSegment(sketch, "E489.direction2", {"start": v(1062.59, -175.18) * mm, "end": v(1062.59, -105.33) * mm, "construction": true});
            skLineSegment(sketch, "E490.bottom", {"start": v(1049.8, -24.54) * mm, "end": v(1067.59, -24.54) * mm});
            skLineSegment(sketch, "E490.top", {"start": v(1049.8, -34.7) * mm, "end": v(1067.59, -34.7) * mm});
            skLineSegment(sketch, "E490.left", {"start": v(1049.8, -24.54) * mm, "end": v(1049.8, -34.7) * mm});
            skLineSegment(sketch, "E490.right", {"start": v(1067.59, -24.54) * mm, "end": v(1067.59, -34.7) * mm});
            skLineSegment(sketch, "E491.MirrorCS", {"start": v(1067.59, -59.13) * mm, "end": v(1067.59, -48.97) * mm});
            skLineSegment(sketch, "E492.MirrorCS", {"start": v(1049.8, -48.97) * mm, "end": v(1067.59, -48.97) * mm});
            skLineSegment(sketch, "E493.MirrorCS", {"start": v(1049.8, -59.13) * mm, "end": v(1049.8, -48.97) * mm});
            skLineSegment(sketch, "E494.MirrorCS", {"start": v(1049.8, -59.13) * mm, "end": v(1067.59, -59.13) * mm});
            skCircle(sketch, "E495", {"center": v(1059.41, -71.9) * mm, "radius": 3.18 * mm});
            skSolve(sketch);
        }
        {
            var Q0;
            Q0 = qSketchRegion(id + "F9", true);
            extrude(context, id + "F10", {"entities" : qUnion([Q0]), "depth" : getVariable(context, 'T0'), "offsetDistance" : 25 * mm});
        }
        {
            var Q0;
            Q0=qCreatedBy(makeId("Top.planeOp"),FACE);
            var sketch = newSketch(context, id + "F11", { "sketchPlane" : qUnion([Q0])});
            skLineSegment(sketch, "E496.bottom", {"start": v(666.51, 160.8) * mm, "end": v(1056.9, 160.8) * mm});
            skLineSegment(sketch, "E496.top", {"start": v(691.9, 148.1) * mm, "end": v(1031.5, 148.1) * mm});
            skLineSegment(sketch, "E496.left", {"start": v(666.5, 160.78) * mm, "end": v(666.5, 148.1) * mm});
            skLineSegment(sketch, "E496.right", {"start": v(1056.9, 160.78) * mm, "end": v(1056.9, 148.1) * mm});
            skPoint(sketch, "E497.visualSharp", {"position": v(666.5, 160.8) * mm});
            skArc(sketch, "E497.filletArc", {"start": v(666.51, 160.8) * mm, "mid": v(666.5, 160.79) * mm, "end": v(666.5, 160.78) * mm});
            skPoint(sketch, "E498.visualSharp", {"position": v(1056.9, 160.8) * mm});
            skArc(sketch, "E498.filletArc", {"start": v(1056.9, 160.78) * mm, "mid": v(1056.9, 160.79) * mm, "end": v(1056.9, 160.8) * mm});
            skLineSegment(sketch, "E499.top", {"start": v(666.5, 141.74) * mm, "end": v(672.85, 141.74) * mm});
            skLineSegment(sketch, "E499.left", {"start": v(666.5, 148.1) * mm, "end": v(666.5, 141.74) * mm});
            skLineSegment(sketch, "E499.right", {"start": v(691.9, 148.1) * mm, "end": v(691.9, 141.74) * mm});
            skLineSegment(sketch, "E500.top", {"start": v(1056.9, 141.74) * mm, "end": v(1050.55, 141.74) * mm});
            skLineSegment(sketch, "E500.left", {"start": v(1056.9, 148.1) * mm, "end": v(1056.9, 141.74) * mm});
            skLineSegment(sketch, "E500.right", {"start": v(1031.5, 148.1) * mm, "end": v(1031.5, 141.74) * mm});
            skLineSegment(sketch, "E501.top", {"start": v(672.85, 136.4) * mm, "end": v(685.55, 136.4) * mm});
            skLineSegment(sketch, "E501.left", {"start": v(672.85, 141.74) * mm, "end": v(672.85, 136.4) * mm});
            skLineSegment(sketch, "E501.right", {"start": v(685.55, 141.74) * mm, "end": v(685.55, 136.4) * mm});
            skLineSegment(sketch, "E502", {"start": v(861.7, 160.8) * mm, "end": v(861.7, 148.1) * mm, "construction": true});
            skLineSegment(sketch, "E503.MirrorCS", {"start": v(1050.55, 141.74) * mm, "end": v(1050.55, 136.4) * mm});
            skLineSegment(sketch, "E504.MirrorCS", {"start": v(1050.55, 136.4) * mm, "end": v(1037.85, 136.4) * mm});
            skLineSegment(sketch, "E505.MirrorCS", {"start": v(1037.85, 141.74) * mm, "end": v(1037.85, 136.4) * mm});
            skLineSegment(sketch, "E506.trimOffspring", {"start": v(1037.85, 141.74) * mm, "end": v(1031.5, 141.74) * mm});
            skLineSegment(sketch, "E507.trimOffspring", {"start": v(685.55, 141.74) * mm, "end": v(691.9, 141.74) * mm});
            skLineSegment(sketch, "E508.bottom", {"start": v(704.08, 238.48) * mm, "end": v(854.46, 238.48) * mm});
            skLineSegment(sketch, "E508.top", {"start": v(729.47, 225.78) * mm, "end": v(829.07, 225.78) * mm});
            skLineSegment(sketch, "E508.left", {"start": v(704.07, 238.47) * mm, "end": v(704.07, 225.78) * mm});
            skLineSegment(sketch, "E508.right", {"start": v(854.47, 238.47) * mm, "end": v(854.47, 225.78) * mm});
            skPoint(sketch, "E509.visualSharp", {"position": v(704.07, 238.48) * mm});
            skArc(sketch, "E509.filletArc", {"start": v(704.08, 238.48) * mm, "mid": v(704.07, 238.48) * mm, "end": v(704.07, 238.47) * mm});
            skPoint(sketch, "E510.visualSharp", {"position": v(854.47, 238.48) * mm});
            skArc(sketch, "E510.filletArc", {"start": v(854.47, 238.47) * mm, "mid": v(854.46, 238.48) * mm, "end": v(854.46, 238.48) * mm});
            skLineSegment(sketch, "E511.top", {"start": v(704.07, 219.43) * mm, "end": v(710.42, 219.43) * mm});
            skLineSegment(sketch, "E511.left", {"start": v(704.07, 225.78) * mm, "end": v(704.07, 219.43) * mm});
            skLineSegment(sketch, "E511.right", {"start": v(729.47, 225.78) * mm, "end": v(729.47, 219.43) * mm});
            skLineSegment(sketch, "E512.top", {"start": v(854.47, 219.43) * mm, "end": v(848.12, 219.43) * mm});
            skLineSegment(sketch, "E512.left", {"start": v(854.47, 225.78) * mm, "end": v(854.47, 219.43) * mm});
            skLineSegment(sketch, "E512.right", {"start": v(829.07, 225.78) * mm, "end": v(829.07, 219.43) * mm});
            skLineSegment(sketch, "E513.top", {"start": v(710.42, 214.1) * mm, "end": v(723.12, 214.1) * mm});
            skLineSegment(sketch, "E513.left", {"start": v(710.42, 219.43) * mm, "end": v(710.42, 214.1) * mm});
            skLineSegment(sketch, "E513.right", {"start": v(723.12, 219.43) * mm, "end": v(723.12, 214.1) * mm});
            skLineSegment(sketch, "E514", {"start": v(779.27, 238.48) * mm, "end": v(779.27, 225.78) * mm, "construction": true});
            skLineSegment(sketch, "E515.MirrorCS", {"start": v(848.12, 219.43) * mm, "end": v(848.12, 214.1) * mm});
            skLineSegment(sketch, "E516.MirrorCS", {"start": v(848.12, 214.1) * mm, "end": v(835.42, 214.1) * mm});
            skLineSegment(sketch, "E517.MirrorCS", {"start": v(835.42, 219.43) * mm, "end": v(835.42, 214.1) * mm});
            skLineSegment(sketch, "E518.trimOffspring", {"start": v(835.42, 219.43) * mm, "end": v(829.07, 219.43) * mm});
            skLineSegment(sketch, "E519.trimOffspring", {"start": v(723.12, 219.43) * mm, "end": v(729.47, 219.43) * mm});
            skLineSegment(sketch, "E520.bottom", {"start": v(872.86, 252.4) * mm, "end": v(1158.24, 252.4) * mm});
            skLineSegment(sketch, "E520.top", {"start": v(898.25, 239.7) * mm, "end": v(1132.85, 239.7) * mm});
            skLineSegment(sketch, "E520.left", {"start": v(872.85, 252.4) * mm, "end": v(872.85, 239.7) * mm});
            skLineSegment(sketch, "E520.right", {"start": v(1158.25, 252.4) * mm, "end": v(1158.25, 239.7) * mm});
            skPoint(sketch, "E521.visualSharp", {"position": v(872.85, 252.4) * mm});
            skArc(sketch, "E521.filletArc", {"start": v(872.86, 252.4) * mm, "mid": v(872.86, 252.4) * mm, "end": v(872.85, 252.4) * mm});
            skPoint(sketch, "E522.visualSharp", {"position": v(1158.25, 252.4) * mm});
            skArc(sketch, "E522.filletArc", {"start": v(1158.25, 252.4) * mm, "mid": v(1158.25, 252.4) * mm, "end": v(1158.24, 252.4) * mm});
            skLineSegment(sketch, "E523.top", {"start": v(872.85, 233.35) * mm, "end": v(879.2, 233.35) * mm});
            skLineSegment(sketch, "E523.left", {"start": v(872.85, 239.7) * mm, "end": v(872.85, 233.35) * mm});
            skLineSegment(sketch, "E523.right", {"start": v(898.25, 239.7) * mm, "end": v(898.25, 233.35) * mm});
            skLineSegment(sketch, "E524.top", {"start": v(1158.25, 233.35) * mm, "end": v(1151.9, 233.35) * mm});
            skLineSegment(sketch, "E524.left", {"start": v(1158.25, 239.7) * mm, "end": v(1158.25, 233.35) * mm});
            skLineSegment(sketch, "E524.right", {"start": v(1132.85, 239.7) * mm, "end": v(1132.85, 233.35) * mm});
            skLineSegment(sketch, "E525.top", {"start": v(879.2, 228.02) * mm, "end": v(891.9, 228.02) * mm});
            skLineSegment(sketch, "E525.left", {"start": v(879.2, 233.35) * mm, "end": v(879.2, 228.02) * mm});
            skLineSegment(sketch, "E525.right", {"start": v(891.9, 233.35) * mm, "end": v(891.9, 228.02) * mm});
            skLineSegment(sketch, "E526", {"start": v(1015.55, 252.4) * mm, "end": v(1015.55, 239.7) * mm, "construction": true});
            skLineSegment(sketch, "E527.MirrorCS", {"start": v(1151.9, 233.35) * mm, "end": v(1151.9, 228.02) * mm});
            skLineSegment(sketch, "E528.MirrorCS", {"start": v(1151.9, 228.02) * mm, "end": v(1139.2, 228.02) * mm});
            skLineSegment(sketch, "E529.MirrorCS", {"start": v(1139.2, 233.35) * mm, "end": v(1139.2, 228.02) * mm});
            skLineSegment(sketch, "E530.trimOffspring", {"start": v(1139.2, 233.35) * mm, "end": v(1132.85, 233.35) * mm});
            skLineSegment(sketch, "E531.trimOffspring", {"start": v(891.9, 233.35) * mm, "end": v(898.25, 233.35) * mm});
            skPoint(sketch, "E532", {"position": v(716.77, 214.1) * mm});
            skPoint(sketch, "E533", {"position": v(841.77, 214.1) * mm});
            skPoint(sketch, "E534", {"position": v(679.2, 136.4) * mm});
            skPoint(sketch, "E535", {"position": v(1044.2, 136.4) * mm});
            skPoint(sketch, "E536", {"position": v(885.55, 228.02) * mm});
            skPoint(sketch, "E537", {"position": v(1145.55, 228.02) * mm});
            skSolve(sketch);
        }
        {
            var Q0;
            Q0 = qSketchRegion(id + "F11", true);
            extrude(context, id + "F12", {"entities" : qUnion([Q0]), "depth" : getVariable(context, 'T0'), "offsetDistance" : 25 * mm});
        }
        {
            var Q0;
            Q0=qCreatedBy(makeId("Top.planeOp"),FACE);
            var sketch = newSketch(context, id + "F13", { "sketchPlane" : qUnion([Q0])});
            skLineSegment(sketch, "E538.bottom", {"start": v(-30.2, 318.82) * mm, "end": v(33.3, 318.82) * mm, "construction": true});
            skLineSegment(sketch, "E538.top", {"start": v(-30.2, 268.02) * mm, "end": v(33.3, 268.02) * mm, "construction": true});
            skLineSegment(sketch, "E538.left", {"start": v(-30.2, 318.82) * mm, "end": v(-30.2, 268.02) * mm, "construction": true});
            skLineSegment(sketch, "E538.right", {"start": v(33.3, 318.82) * mm, "end": v(33.3, 268.02) * mm, "construction": true});
            skLineSegment(sketch, "E539.bottom", {"start": v(-31.55, 325.17) * mm, "end": v(34.65, 325.17) * mm});
            skLineSegment(sketch, "E539.top", {"start": v(-31.55, 261.67) * mm, "end": v(34.65, 261.67) * mm});
            skLineSegment(sketch, "E539.left", {"start": v(-36.55, 320.17) * mm, "end": v(-36.55, 266.67) * mm});
            skLineSegment(sketch, "E539.right", {"start": v(39.65, 320.17) * mm, "end": v(39.65, 266.67) * mm});
            skCircle(sketch, "E540", {"center": v(33.3, 268.02) * mm, "radius": 1.59 * mm});
            skCircle(sketch, "E541", {"center": v(33.3, 318.82) * mm, "radius": 1.59 * mm});
            skCircle(sketch, "E542", {"center": v(-30.2, 268.02) * mm, "radius": 1.6 * mm});
            skCircle(sketch, "E543", {"center": v(-30.2, 318.82) * mm, "radius": 1.6 * mm});
            skPoint(sketch, "E544.visualSharp", {"position": v(39.65, 325.17) * mm});
            skArc(sketch, "E544.filletArc", {"start": v(39.65, 320.17) * mm, "mid": v(38.19, 323.7) * mm, "end": v(34.65, 325.17) * mm});
            skPoint(sketch, "E545.visualSharp", {"position": v(39.65, 261.67) * mm});
            skArc(sketch, "E545.filletArc", {"start": v(34.65, 261.67) * mm, "mid": v(38.19, 263.13) * mm, "end": v(39.65, 266.67) * mm});
            skPoint(sketch, "E546.visualSharp", {"position": v(-36.55, 325.17) * mm});
            skArc(sketch, "E546.filletArc", {"start": v(-31.55, 325.17) * mm, "mid": v(-35.08, 323.7) * mm, "end": v(-36.55, 320.17) * mm});
            skPoint(sketch, "E547.visualSharp", {"position": v(-36.55, 261.67) * mm});
            skArc(sketch, "E547.filletArc", {"start": v(-36.55, 266.67) * mm, "mid": v(-35.08, 263.13) * mm, "end": v(-31.55, 261.67) * mm});
            skLineSegment(sketch, "E548", {"start": v(-36.55, 293.42) * mm, "end": v(39.65, 293.42) * mm, "construction": true});
            skLineSegment(sketch, "E549", {"start": v(1.55, 325.17) * mm, "end": v(1.55, 261.67) * mm, "construction": true});
            skCircle(sketch, "E550", {"center": v(1.55, 293.42) * mm, "radius": 3.75 * mm});
            skCircle(sketch, "E551", {"center": v(1.55, 309.93) * mm, "radius": 3.75 * mm});
            skCircle(sketch, "E552", {"center": v(1.55, 276.9) * mm, "radius": 3.75 * mm});
            skCircle(sketch, "E553", {"center": v(19.33, 293.42) * mm, "radius": 3.75 * mm});
            skCircle(sketch, "E554", {"center": v(-18.26, 293.42) * mm, "radius": 3.75 * mm});
            skLineSegment(sketch, "E555.bottom", {"start": v(-163.22, 315.49) * mm, "end": v(-99.72, 315.49) * mm, "construction": true});
            skLineSegment(sketch, "E555.top", {"start": v(-163.22, 264.69) * mm, "end": v(-99.72, 264.69) * mm, "construction": true});
            skLineSegment(sketch, "E555.left", {"start": v(-163.22, 315.49) * mm, "end": v(-163.22, 264.69) * mm, "construction": true});
            skLineSegment(sketch, "E555.right", {"start": v(-99.72, 315.49) * mm, "end": v(-99.72, 264.69) * mm, "construction": true});
            skLineSegment(sketch, "E556.bottom", {"start": v(-164.57, 321.84) * mm, "end": v(-98.37, 321.84) * mm});
            skLineSegment(sketch, "E556.top", {"start": v(-164.57, 258.34) * mm, "end": v(-98.37, 258.34) * mm});
            skLineSegment(sketch, "E556.left", {"start": v(-169.57, 316.84) * mm, "end": v(-169.57, 263.34) * mm});
            skLineSegment(sketch, "E556.right", {"start": v(-93.37, 316.84) * mm, "end": v(-93.37, 263.34) * mm});
            skCircle(sketch, "E557", {"center": v(-99.72, 264.69) * mm, "radius": 1.59 * mm});
            skCircle(sketch, "E558", {"center": v(-99.72, 315.49) * mm, "radius": 1.59 * mm});
            skCircle(sketch, "E559", {"center": v(-163.22, 264.69) * mm, "radius": 1.6 * mm});
            skCircle(sketch, "E560", {"center": v(-163.22, 315.49) * mm, "radius": 1.6 * mm});
            skPoint(sketch, "E561.visualSharp", {"position": v(-93.37, 321.84) * mm});
            skArc(sketch, "E561.filletArc", {"start": v(-93.37, 316.84) * mm, "mid": v(-94.83, 320.37) * mm, "end": v(-98.37, 321.84) * mm});
            skPoint(sketch, "E562.visualSharp", {"position": v(-93.37, 258.34) * mm});
            skArc(sketch, "E562.filletArc", {"start": v(-98.37, 258.34) * mm, "mid": v(-94.83, 259.8) * mm, "end": v(-93.37, 263.34) * mm});
            skPoint(sketch, "E563.visualSharp", {"position": v(-169.57, 321.84) * mm});
            skArc(sketch, "E563.filletArc", {"start": v(-164.57, 321.84) * mm, "mid": v(-168.1, 320.37) * mm, "end": v(-169.57, 316.84) * mm});
            skPoint(sketch, "E564.visualSharp", {"position": v(-169.57, 258.34) * mm});
            skArc(sketch, "E564.filletArc", {"start": v(-169.57, 263.34) * mm, "mid": v(-168.1, 259.8) * mm, "end": v(-164.57, 258.34) * mm});
            skLineSegment(sketch, "E565", {"start": v(-169.57, 290.09) * mm, "end": v(-93.37, 290.09) * mm, "construction": true});
            skLineSegment(sketch, "E566", {"start": v(-131.47, 321.84) * mm, "end": v(-131.47, 258.34) * mm, "construction": true});
            skLineSegment(sketch, "E567.bottom", {"start": v(-102.78, 311.5) * mm, "end": v(-128.77, 311.5) * mm});
            skLineSegment(sketch, "E567.top", {"start": v(-102.78, 268.68) * mm, "end": v(-128.77, 268.68) * mm});
            skLineSegment(sketch, "E567.left", {"start": v(-102.78, 311.5) * mm, "end": v(-102.78, 268.68) * mm});
            skLineSegment(sketch, "E567.right", {"start": v(-160.15, 311.5) * mm, "end": v(-160.15, 268.68) * mm});
            skPoint(sketch, "E567.middle", {"position": v(-131.47, 290.09) * mm});
            skCircle(sketch, "E568", {"center": v(-131.47, 307.87) * mm, "radius": 1.59 * mm});
            skCircle(sketch, "E569.MirrorC", {"center": v(-131.47, 272.3) * mm, "radius": 1.59 * mm});
            skArc(sketch, "E570", {"start": v(-134.17, 307.87) * mm, "mid": v(-131.47, 305.17) * mm, "end": v(-128.77, 307.87) * mm});
            skLineSegment(sketch, "E571", {"start": v(-134.17, 307.87) * mm, "end": v(-134.17, 311.5) * mm});
            skLineSegment(sketch, "E572", {"start": v(-128.77, 307.87) * mm, "end": v(-128.77, 311.5) * mm});
            skLineSegment(sketch, "E573.trimOffspring", {"start": v(-134.17, 311.5) * mm, "end": v(-160.15, 311.5) * mm});
            skLineSegment(sketch, "E574.MirrorCS", {"start": v(-128.77, 272.3) * mm, "end": v(-128.77, 268.68) * mm});
            skArc(sketch, "E575.MirrorCS", {"start": v(-134.17, 272.3) * mm, "mid": v(-131.47, 275) * mm, "end": v(-128.77, 272.3) * mm});
            skLineSegment(sketch, "E576.MirrorCS", {"start": v(-134.17, 272.3) * mm, "end": v(-134.17, 268.68) * mm});
            skLineSegment(sketch, "E577.trimOffspring", {"start": v(-134.17, 268.68) * mm, "end": v(-160.15, 268.68) * mm});
            skSolve(sketch);
        }
        {
            var Q0;
            Q0 = qSketchRegion(id + "F13", true);
            extrude(context, id + "F14", {"entities" : qUnion([Q0]), "depth" : getVariable(context, 'T0'), "offsetDistance" : 25 * mm});
        }
    });
